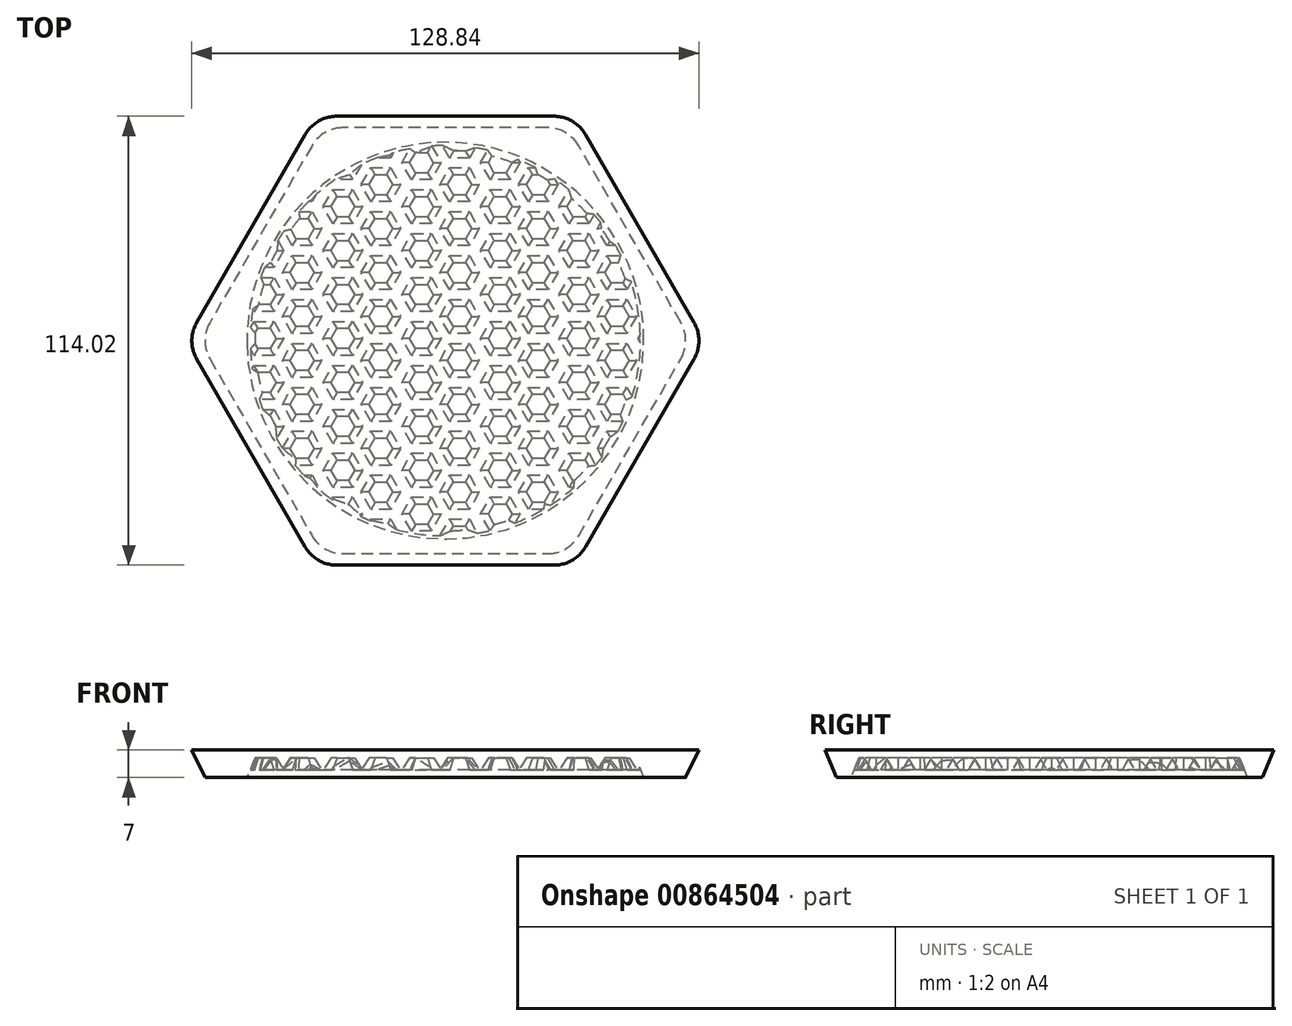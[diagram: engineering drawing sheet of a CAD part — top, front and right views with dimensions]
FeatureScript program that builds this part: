
annotation { "Feature Type Name" : "Feature", "Feature Type Description" : "" }
export const myFeature = defineFeature(function(context is Context, id is Id, definition is map)
    precondition{}
    {
        {
            var Q0;
            Q0=qCreatedBy(makeId("Top.planeOp"),FACE);
            var sketch = newSketch(context, id + "F0", { "sketchPlane" : qUnion([Q0])});
            skCircle(sketch, "E0.cCircle", {"center": v(0, 0) * mm, "radius": 62.5 * mm, "construction": true});
            skLineSegment(sketch, "E0.0", {"start": v(62.5, 0) * mm, "end": v(31.25, -54.13) * mm});
            skLineSegment(sketch, "E0.1", {"start": v(31.25, -54.13) * mm, "end": v(-31.25, -54.13) * mm});
            skLineSegment(sketch, "E0.2", {"start": v(-31.25, -54.13) * mm, "end": v(-62.5, 0) * mm});
            skLineSegment(sketch, "E0.3", {"start": v(-62.5, 0) * mm, "end": v(-31.25, 54.13) * mm});
            skLineSegment(sketch, "E0.4", {"start": v(-31.25, 54.13) * mm, "end": v(31.25, 54.13) * mm});
            skLineSegment(sketch, "E0.5", {"start": v(31.25, 54.13) * mm, "end": v(62.5, 0) * mm});
            skSolve(sketch);
        }
        {
            var Q0;
            Q0 = qSketchRegion(id + "F0", true);
            extrude(context, id + "F1", {"entities" : qUnion([Q0]), "depth" : 5 * mm, "offsetDistance" : 25 * mm, "hasDraft" : true, "draftAngle" : 30 * degree});
        }
        {
            var Q0;
            Q0=makeQuery(id+"F1.opExtrude","CAP_FACE",FACE,{"disambiguationData":[OSD([sQuery(id+"F0.wireOp",EDGE,"E0.0"),sQuery(id+"F0.wireOp",EDGE,"E0.1"),sQuery(id+"F0.wireOp",EDGE,"E0.2"),sQuery(id+"F0.wireOp",EDGE,"E0.3"),sQuery(id+"F0.wireOp",EDGE,"E0.4"),sQuery(id+"F0.wireOp",EDGE,"E0.5")])],"isStart":true});
            var sketch = newSketch(context, id + "F2", { "sketchPlane" : qUnion([Q0])});
            skCircle(sketch, "E1.cCircle", {"center": v(63.6, 60.82) * mm, "radius": 5 * mm, "construction": true});
            skLineSegment(sketch, "E1.0", {"start": v(58.6, 60.82) * mm, "end": v(61.1, 65.15) * mm});
            skLineSegment(sketch, "E1.1", {"start": v(61.1, 65.15) * mm, "end": v(66.1, 65.15) * mm});
            skLineSegment(sketch, "E1.2", {"start": v(66.1, 65.15) * mm, "end": v(68.6, 60.82) * mm});
            skLineSegment(sketch, "E1.3", {"start": v(68.6, 60.82) * mm, "end": v(66.1, 56.49) * mm});
            skLineSegment(sketch, "E1.4", {"start": v(66.1, 56.49) * mm, "end": v(61.1, 56.49) * mm});
            skLineSegment(sketch, "E1.5", {"start": v(61.1, 56.49) * mm, "end": v(58.6, 60.82) * mm});
            skCircle(sketch, "E2.cCircle", {"center": v(53.94, 66.4) * mm, "radius": 5 * mm, "construction": true});
            skLineSegment(sketch, "E2.0", {"start": v(48.94, 66.4) * mm, "end": v(51.44, 70.73) * mm});
            skLineSegment(sketch, "E2.1", {"start": v(51.44, 70.73) * mm, "end": v(56.44, 70.73) * mm});
            skLineSegment(sketch, "E2.2", {"start": v(56.44, 70.73) * mm, "end": v(58.94, 66.4) * mm});
            skLineSegment(sketch, "E2.3", {"start": v(58.94, 66.4) * mm, "end": v(56.44, 62.07) * mm});
            skLineSegment(sketch, "E2.4", {"start": v(56.44, 62.07) * mm, "end": v(51.44, 62.07) * mm});
            skLineSegment(sketch, "E2.5", {"start": v(51.44, 62.07) * mm, "end": v(48.94, 66.4) * mm});
            skLineSegment(sketch, "E3.0.1.0", {"start": v(51.44, 50.9) * mm, "end": v(48.94, 55.24) * mm});
            skCircle(sketch, "E3.0.1.1", {"center": v(63.6, 49.66) * mm, "radius": 5 * mm, "construction": true});
            skLineSegment(sketch, "E3.0.1.2", {"start": v(61.1, 53.99) * mm, "end": v(66.1, 53.99) * mm});
            skLineSegment(sketch, "E3.0.1.3", {"start": v(68.6, 49.66) * mm, "end": v(66.1, 45.33) * mm});
            skLineSegment(sketch, "E3.0.1.4", {"start": v(58.94, 55.24) * mm, "end": v(56.44, 50.9) * mm});
            skLineSegment(sketch, "E3.0.1.5", {"start": v(56.44, 59.57) * mm, "end": v(58.94, 55.24) * mm});
            skLineSegment(sketch, "E3.0.1.6", {"start": v(51.44, 59.57) * mm, "end": v(56.44, 59.57) * mm});
            skLineSegment(sketch, "E3.0.1.7", {"start": v(56.44, 50.9) * mm, "end": v(51.44, 50.9) * mm});
            skLineSegment(sketch, "E3.0.1.8", {"start": v(66.1, 53.99) * mm, "end": v(68.6, 49.66) * mm});
            skCircle(sketch, "E3.0.1.9", {"center": v(53.94, 55.24) * mm, "radius": 5 * mm, "construction": true});
            skLineSegment(sketch, "E3.0.1.10", {"start": v(48.94, 55.24) * mm, "end": v(51.44, 59.57) * mm});
            skLineSegment(sketch, "E3.0.1.11", {"start": v(61.1, 45.33) * mm, "end": v(58.6, 49.66) * mm});
            skLineSegment(sketch, "E3.0.1.12", {"start": v(66.1, 45.33) * mm, "end": v(61.1, 45.33) * mm});
            skLineSegment(sketch, "E3.0.1.13", {"start": v(58.6, 49.66) * mm, "end": v(61.1, 53.99) * mm});
            skLineSegment(sketch, "E3.0.2.0", {"start": v(51.44, 39.75) * mm, "end": v(48.94, 44.08) * mm});
            skCircle(sketch, "E3.0.2.1", {"center": v(63.6, 38.5) * mm, "radius": 5 * mm, "construction": true});
            skLineSegment(sketch, "E3.0.2.2", {"start": v(61.1, 42.83) * mm, "end": v(66.1, 42.83) * mm});
            skLineSegment(sketch, "E3.0.2.3", {"start": v(68.6, 38.5) * mm, "end": v(66.1, 34.17) * mm});
            skLineSegment(sketch, "E3.0.2.4", {"start": v(58.94, 44.08) * mm, "end": v(56.44, 39.75) * mm});
            skLineSegment(sketch, "E3.0.2.5", {"start": v(56.44, 48.4) * mm, "end": v(58.94, 44.08) * mm});
            skLineSegment(sketch, "E3.0.2.6", {"start": v(51.44, 48.4) * mm, "end": v(56.44, 48.4) * mm});
            skLineSegment(sketch, "E3.0.2.7", {"start": v(56.44, 39.75) * mm, "end": v(51.44, 39.75) * mm});
            skLineSegment(sketch, "E3.0.2.8", {"start": v(66.1, 42.83) * mm, "end": v(68.6, 38.5) * mm});
            skCircle(sketch, "E3.0.2.9", {"center": v(53.94, 44.08) * mm, "radius": 5 * mm, "construction": true});
            skLineSegment(sketch, "E3.0.2.10", {"start": v(48.94, 44.08) * mm, "end": v(51.44, 48.4) * mm});
            skLineSegment(sketch, "E3.0.2.11", {"start": v(61.1, 34.17) * mm, "end": v(58.6, 38.5) * mm});
            skLineSegment(sketch, "E3.0.2.12", {"start": v(66.1, 34.17) * mm, "end": v(61.1, 34.17) * mm});
            skLineSegment(sketch, "E3.0.2.13", {"start": v(58.6, 38.5) * mm, "end": v(61.1, 42.83) * mm});
            skLineSegment(sketch, "E3.0.3.0", {"start": v(51.44, 28.59) * mm, "end": v(48.94, 32.92) * mm});
            skCircle(sketch, "E3.0.3.1", {"center": v(63.6, 27.34) * mm, "radius": 5 * mm, "construction": true});
            skLineSegment(sketch, "E3.0.3.2", {"start": v(61.1, 31.67) * mm, "end": v(66.1, 31.67) * mm});
            skLineSegment(sketch, "E3.0.3.3", {"start": v(68.6, 27.34) * mm, "end": v(66.1, 23) * mm});
            skLineSegment(sketch, "E3.0.3.4", {"start": v(58.94, 32.92) * mm, "end": v(56.44, 28.59) * mm});
            skLineSegment(sketch, "E3.0.3.5", {"start": v(56.44, 37.25) * mm, "end": v(58.94, 32.92) * mm});
            skLineSegment(sketch, "E3.0.3.6", {"start": v(51.44, 37.25) * mm, "end": v(56.44, 37.25) * mm});
            skLineSegment(sketch, "E3.0.3.7", {"start": v(56.44, 28.59) * mm, "end": v(51.44, 28.59) * mm});
            skLineSegment(sketch, "E3.0.3.8", {"start": v(66.1, 31.67) * mm, "end": v(68.6, 27.34) * mm});
            skCircle(sketch, "E3.0.3.9", {"center": v(53.94, 32.92) * mm, "radius": 5 * mm, "construction": true});
            skLineSegment(sketch, "E3.0.3.10", {"start": v(48.94, 32.92) * mm, "end": v(51.44, 37.25) * mm});
            skLineSegment(sketch, "E3.0.3.11", {"start": v(61.1, 23) * mm, "end": v(58.6, 27.34) * mm});
            skLineSegment(sketch, "E3.0.3.12", {"start": v(66.1, 23) * mm, "end": v(61.1, 23) * mm});
            skLineSegment(sketch, "E3.0.3.13", {"start": v(58.6, 27.34) * mm, "end": v(61.1, 31.67) * mm});
            skLineSegment(sketch, "E3.0.4.0", {"start": v(51.44, 17.43) * mm, "end": v(48.94, 21.76) * mm});
            skCircle(sketch, "E3.0.4.1", {"center": v(63.6, 16.18) * mm, "radius": 5 * mm, "construction": true});
            skLineSegment(sketch, "E3.0.4.2", {"start": v(61.1, 20.5) * mm, "end": v(66.1, 20.5) * mm});
            skLineSegment(sketch, "E3.0.4.3", {"start": v(68.6, 16.18) * mm, "end": v(66.1, 11.85) * mm});
            skLineSegment(sketch, "E3.0.4.4", {"start": v(58.94, 21.76) * mm, "end": v(56.44, 17.43) * mm});
            skLineSegment(sketch, "E3.0.4.5", {"start": v(56.44, 26.09) * mm, "end": v(58.94, 21.76) * mm});
            skLineSegment(sketch, "E3.0.4.6", {"start": v(51.44, 26.09) * mm, "end": v(56.44, 26.09) * mm});
            skLineSegment(sketch, "E3.0.4.7", {"start": v(56.44, 17.43) * mm, "end": v(51.44, 17.43) * mm});
            skLineSegment(sketch, "E3.0.4.8", {"start": v(66.1, 20.5) * mm, "end": v(68.6, 16.18) * mm});
            skCircle(sketch, "E3.0.4.9", {"center": v(53.94, 21.76) * mm, "radius": 5 * mm, "construction": true});
            skLineSegment(sketch, "E3.0.4.10", {"start": v(48.94, 21.76) * mm, "end": v(51.44, 26.09) * mm});
            skLineSegment(sketch, "E3.0.4.11", {"start": v(61.1, 11.85) * mm, "end": v(58.6, 16.18) * mm});
            skLineSegment(sketch, "E3.0.4.12", {"start": v(66.1, 11.85) * mm, "end": v(61.1, 11.85) * mm});
            skLineSegment(sketch, "E3.0.4.13", {"start": v(58.6, 16.18) * mm, "end": v(61.1, 20.5) * mm});
            skLineSegment(sketch, "E3.0.5.0", {"start": v(51.44, 6.27) * mm, "end": v(48.94, 10.6) * mm});
            skCircle(sketch, "E3.0.5.1", {"center": v(63.6, 5.02) * mm, "radius": 5 * mm, "construction": true});
            skLineSegment(sketch, "E3.0.5.2", {"start": v(61.1, 9.35) * mm, "end": v(66.1, 9.35) * mm});
            skLineSegment(sketch, "E3.0.5.3", {"start": v(68.6, 5.02) * mm, "end": v(66.1, 0.69) * mm});
            skLineSegment(sketch, "E3.0.5.4", {"start": v(58.94, 10.6) * mm, "end": v(56.44, 6.27) * mm});
            skLineSegment(sketch, "E3.0.5.5", {"start": v(56.44, 14.93) * mm, "end": v(58.94, 10.6) * mm});
            skLineSegment(sketch, "E3.0.5.6", {"start": v(51.44, 14.93) * mm, "end": v(56.44, 14.93) * mm});
            skLineSegment(sketch, "E3.0.5.7", {"start": v(56.44, 6.27) * mm, "end": v(51.44, 6.27) * mm});
            skLineSegment(sketch, "E3.0.5.8", {"start": v(66.1, 9.35) * mm, "end": v(68.6, 5.02) * mm});
            skCircle(sketch, "E3.0.5.9", {"center": v(53.94, 10.6) * mm, "radius": 5 * mm, "construction": true});
            skLineSegment(sketch, "E3.0.5.10", {"start": v(48.94, 10.6) * mm, "end": v(51.44, 14.93) * mm});
            skLineSegment(sketch, "E3.0.5.11", {"start": v(61.1, 0.69) * mm, "end": v(58.6, 5.02) * mm});
            skLineSegment(sketch, "E3.0.5.12", {"start": v(66.1, 0.69) * mm, "end": v(61.1, 0.69) * mm});
            skLineSegment(sketch, "E3.0.5.13", {"start": v(58.6, 5.02) * mm, "end": v(61.1, 9.35) * mm});
            skLineSegment(sketch, "E3.0.6.0", {"start": v(51.44, -4.9) * mm, "end": v(48.94, -0.56) * mm});
            skCircle(sketch, "E3.0.6.1", {"center": v(63.6, -6.14) * mm, "radius": 5 * mm, "construction": true});
            skLineSegment(sketch, "E3.0.6.2", {"start": v(61.1, -1.81) * mm, "end": v(66.1, -1.81) * mm});
            skLineSegment(sketch, "E3.0.6.3", {"start": v(68.6, -6.14) * mm, "end": v(66.1, -10.47) * mm});
            skLineSegment(sketch, "E3.0.6.4", {"start": v(58.94, -0.56) * mm, "end": v(56.44, -4.9) * mm});
            skLineSegment(sketch, "E3.0.6.5", {"start": v(56.44, 3.77) * mm, "end": v(58.94, -0.56) * mm});
            skLineSegment(sketch, "E3.0.6.6", {"start": v(51.44, 3.77) * mm, "end": v(56.44, 3.77) * mm});
            skLineSegment(sketch, "E3.0.6.7", {"start": v(56.44, -4.9) * mm, "end": v(51.44, -4.9) * mm});
            skLineSegment(sketch, "E3.0.6.8", {"start": v(66.1, -1.81) * mm, "end": v(68.6, -6.14) * mm});
            skCircle(sketch, "E3.0.6.9", {"center": v(53.94, -0.56) * mm, "radius": 5 * mm, "construction": true});
            skLineSegment(sketch, "E3.0.6.10", {"start": v(48.94, -0.56) * mm, "end": v(51.44, 3.77) * mm});
            skLineSegment(sketch, "E3.0.6.11", {"start": v(61.1, -10.47) * mm, "end": v(58.6, -6.14) * mm});
            skLineSegment(sketch, "E3.0.6.12", {"start": v(66.1, -10.47) * mm, "end": v(61.1, -10.47) * mm});
            skLineSegment(sketch, "E3.0.6.13", {"start": v(58.6, -6.14) * mm, "end": v(61.1, -1.81) * mm});
            skLineSegment(sketch, "E3.0.7.0", {"start": v(51.44, -16.05) * mm, "end": v(48.94, -11.72) * mm});
            skCircle(sketch, "E3.0.7.1", {"center": v(63.6, -17.3) * mm, "radius": 5 * mm, "construction": true});
            skLineSegment(sketch, "E3.0.7.2", {"start": v(61.1, -12.97) * mm, "end": v(66.1, -12.97) * mm});
            skLineSegment(sketch, "E3.0.7.3", {"start": v(68.6, -17.3) * mm, "end": v(66.1, -21.63) * mm});
            skLineSegment(sketch, "E3.0.7.4", {"start": v(58.94, -11.72) * mm, "end": v(56.44, -16.05) * mm});
            skLineSegment(sketch, "E3.0.7.5", {"start": v(56.44, -7.4) * mm, "end": v(58.94, -11.72) * mm});
            skLineSegment(sketch, "E3.0.7.6", {"start": v(51.44, -7.4) * mm, "end": v(56.44, -7.4) * mm});
            skLineSegment(sketch, "E3.0.7.7", {"start": v(56.44, -16.05) * mm, "end": v(51.44, -16.05) * mm});
            skLineSegment(sketch, "E3.0.7.8", {"start": v(66.1, -12.97) * mm, "end": v(68.6, -17.3) * mm});
            skCircle(sketch, "E3.0.7.9", {"center": v(53.94, -11.72) * mm, "radius": 5 * mm, "construction": true});
            skLineSegment(sketch, "E3.0.7.10", {"start": v(48.94, -11.72) * mm, "end": v(51.44, -7.4) * mm});
            skLineSegment(sketch, "E3.0.7.11", {"start": v(61.1, -21.63) * mm, "end": v(58.6, -17.3) * mm});
            skLineSegment(sketch, "E3.0.7.12", {"start": v(66.1, -21.63) * mm, "end": v(61.1, -21.63) * mm});
            skLineSegment(sketch, "E3.0.7.13", {"start": v(58.6, -17.3) * mm, "end": v(61.1, -12.97) * mm});
            skLineSegment(sketch, "E3.0.8.0", {"start": v(51.44, -27.21) * mm, "end": v(48.94, -22.88) * mm});
            skCircle(sketch, "E3.0.8.1", {"center": v(63.6, -28.46) * mm, "radius": 5 * mm, "construction": true});
            skLineSegment(sketch, "E3.0.8.2", {"start": v(61.1, -24.13) * mm, "end": v(66.1, -24.13) * mm});
            skLineSegment(sketch, "E3.0.8.3", {"start": v(68.6, -28.46) * mm, "end": v(66.1, -32.8) * mm});
            skLineSegment(sketch, "E3.0.8.4", {"start": v(58.94, -22.88) * mm, "end": v(56.44, -27.21) * mm});
            skLineSegment(sketch, "E3.0.8.5", {"start": v(56.44, -18.55) * mm, "end": v(58.94, -22.88) * mm});
            skLineSegment(sketch, "E3.0.8.6", {"start": v(51.44, -18.55) * mm, "end": v(56.44, -18.55) * mm});
            skLineSegment(sketch, "E3.0.8.7", {"start": v(56.44, -27.21) * mm, "end": v(51.44, -27.21) * mm});
            skLineSegment(sketch, "E3.0.8.8", {"start": v(66.1, -24.13) * mm, "end": v(68.6, -28.46) * mm});
            skCircle(sketch, "E3.0.8.9", {"center": v(53.94, -22.88) * mm, "radius": 5 * mm, "construction": true});
            skLineSegment(sketch, "E3.0.8.10", {"start": v(48.94, -22.88) * mm, "end": v(51.44, -18.55) * mm});
            skLineSegment(sketch, "E3.0.8.11", {"start": v(61.1, -32.8) * mm, "end": v(58.6, -28.46) * mm});
            skLineSegment(sketch, "E3.0.8.12", {"start": v(66.1, -32.8) * mm, "end": v(61.1, -32.8) * mm});
            skLineSegment(sketch, "E3.0.8.13", {"start": v(58.6, -28.46) * mm, "end": v(61.1, -24.13) * mm});
            skLineSegment(sketch, "E3.0.9.0", {"start": v(51.44, -38.37) * mm, "end": v(48.94, -34.04) * mm});
            skCircle(sketch, "E3.0.9.1", {"center": v(63.6, -39.62) * mm, "radius": 5 * mm, "construction": true});
            skLineSegment(sketch, "E3.0.9.2", {"start": v(61.1, -35.3) * mm, "end": v(66.1, -35.3) * mm});
            skLineSegment(sketch, "E3.0.9.3", {"start": v(68.6, -39.62) * mm, "end": v(66.1, -43.95) * mm});
            skLineSegment(sketch, "E3.0.9.4", {"start": v(58.94, -34.04) * mm, "end": v(56.44, -38.37) * mm});
            skLineSegment(sketch, "E3.0.9.5", {"start": v(56.44, -29.71) * mm, "end": v(58.94, -34.04) * mm});
            skLineSegment(sketch, "E3.0.9.6", {"start": v(51.44, -29.71) * mm, "end": v(56.44, -29.71) * mm});
            skLineSegment(sketch, "E3.0.9.7", {"start": v(56.44, -38.37) * mm, "end": v(51.44, -38.37) * mm});
            skLineSegment(sketch, "E3.0.9.8", {"start": v(66.1, -35.3) * mm, "end": v(68.6, -39.62) * mm});
            skCircle(sketch, "E3.0.9.9", {"center": v(53.94, -34.04) * mm, "radius": 5 * mm, "construction": true});
            skLineSegment(sketch, "E3.0.9.10", {"start": v(48.94, -34.04) * mm, "end": v(51.44, -29.71) * mm});
            skLineSegment(sketch, "E3.0.9.11", {"start": v(61.1, -43.95) * mm, "end": v(58.6, -39.62) * mm});
            skLineSegment(sketch, "E3.0.9.12", {"start": v(66.1, -43.95) * mm, "end": v(61.1, -43.95) * mm});
            skLineSegment(sketch, "E3.0.9.13", {"start": v(58.6, -39.62) * mm, "end": v(61.1, -35.3) * mm});
            skLineSegment(sketch, "E3.0.10.0", {"start": v(51.44, -49.53) * mm, "end": v(48.94, -45.2) * mm});
            skCircle(sketch, "E3.0.10.1", {"center": v(63.6, -50.78) * mm, "radius": 5 * mm, "construction": true});
            skLineSegment(sketch, "E3.0.10.2", {"start": v(61.1, -46.45) * mm, "end": v(66.1, -46.45) * mm});
            skLineSegment(sketch, "E3.0.10.3", {"start": v(68.6, -50.78) * mm, "end": v(66.1, -55.11) * mm});
            skLineSegment(sketch, "E3.0.10.4", {"start": v(58.94, -45.2) * mm, "end": v(56.44, -49.53) * mm});
            skLineSegment(sketch, "E3.0.10.5", {"start": v(56.44, -40.87) * mm, "end": v(58.94, -45.2) * mm});
            skLineSegment(sketch, "E3.0.10.6", {"start": v(51.44, -40.87) * mm, "end": v(56.44, -40.87) * mm});
            skLineSegment(sketch, "E3.0.10.7", {"start": v(56.44, -49.53) * mm, "end": v(51.44, -49.53) * mm});
            skLineSegment(sketch, "E3.0.10.8", {"start": v(66.1, -46.45) * mm, "end": v(68.6, -50.78) * mm});
            skCircle(sketch, "E3.0.10.9", {"center": v(53.94, -45.2) * mm, "radius": 5 * mm, "construction": true});
            skLineSegment(sketch, "E3.0.10.10", {"start": v(48.94, -45.2) * mm, "end": v(51.44, -40.87) * mm});
            skLineSegment(sketch, "E3.0.10.11", {"start": v(61.1, -55.11) * mm, "end": v(58.6, -50.78) * mm});
            skLineSegment(sketch, "E3.0.10.12", {"start": v(66.1, -55.11) * mm, "end": v(61.1, -55.11) * mm});
            skLineSegment(sketch, "E3.0.10.13", {"start": v(58.6, -50.78) * mm, "end": v(61.1, -46.45) * mm});
            skLineSegment(sketch, "E3.1.0.0", {"start": v(31.44, 62.07) * mm, "end": v(28.94, 66.4) * mm});
            skCircle(sketch, "E3.1.0.1", {"center": v(43.6, 60.82) * mm, "radius": 5 * mm, "construction": true});
            skLineSegment(sketch, "E3.1.0.2", {"start": v(41.1, 65.15) * mm, "end": v(46.1, 65.15) * mm});
            skLineSegment(sketch, "E3.1.0.3", {"start": v(48.6, 60.82) * mm, "end": v(46.1, 56.49) * mm});
            skLineSegment(sketch, "E3.1.0.4", {"start": v(38.94, 66.4) * mm, "end": v(36.44, 62.07) * mm});
            skLineSegment(sketch, "E3.1.0.5", {"start": v(36.44, 70.73) * mm, "end": v(38.94, 66.4) * mm});
            skLineSegment(sketch, "E3.1.0.6", {"start": v(31.44, 70.73) * mm, "end": v(36.44, 70.73) * mm});
            skLineSegment(sketch, "E3.1.0.7", {"start": v(36.44, 62.07) * mm, "end": v(31.44, 62.07) * mm});
            skLineSegment(sketch, "E3.1.0.8", {"start": v(46.1, 65.15) * mm, "end": v(48.6, 60.82) * mm});
            skCircle(sketch, "E3.1.0.9", {"center": v(33.94, 66.4) * mm, "radius": 5 * mm, "construction": true});
            skLineSegment(sketch, "E3.1.0.10", {"start": v(28.94, 66.4) * mm, "end": v(31.44, 70.73) * mm});
            skLineSegment(sketch, "E3.1.0.11", {"start": v(41.1, 56.49) * mm, "end": v(38.6, 60.82) * mm});
            skLineSegment(sketch, "E3.1.0.12", {"start": v(46.1, 56.49) * mm, "end": v(41.1, 56.49) * mm});
            skLineSegment(sketch, "E3.1.0.13", {"start": v(38.6, 60.82) * mm, "end": v(41.1, 65.15) * mm});
            skLineSegment(sketch, "E3.1.1.0", {"start": v(31.44, 50.9) * mm, "end": v(28.94, 55.24) * mm});
            skCircle(sketch, "E3.1.1.1", {"center": v(43.6, 49.66) * mm, "radius": 5 * mm, "construction": true});
            skLineSegment(sketch, "E3.1.1.2", {"start": v(41.1, 53.99) * mm, "end": v(46.1, 53.99) * mm});
            skLineSegment(sketch, "E3.1.1.3", {"start": v(48.6, 49.66) * mm, "end": v(46.1, 45.33) * mm});
            skLineSegment(sketch, "E3.1.1.4", {"start": v(38.94, 55.24) * mm, "end": v(36.44, 50.9) * mm});
            skLineSegment(sketch, "E3.1.1.5", {"start": v(36.44, 59.57) * mm, "end": v(38.94, 55.24) * mm});
            skLineSegment(sketch, "E3.1.1.6", {"start": v(31.44, 59.57) * mm, "end": v(36.44, 59.57) * mm});
            skLineSegment(sketch, "E3.1.1.7", {"start": v(36.44, 50.9) * mm, "end": v(31.44, 50.9) * mm});
            skLineSegment(sketch, "E3.1.1.8", {"start": v(46.1, 53.99) * mm, "end": v(48.6, 49.66) * mm});
            skCircle(sketch, "E3.1.1.9", {"center": v(33.94, 55.24) * mm, "radius": 5 * mm, "construction": true});
            skLineSegment(sketch, "E3.1.1.10", {"start": v(28.94, 55.24) * mm, "end": v(31.44, 59.57) * mm});
            skLineSegment(sketch, "E3.1.1.11", {"start": v(41.1, 45.33) * mm, "end": v(38.6, 49.66) * mm});
            skLineSegment(sketch, "E3.1.1.12", {"start": v(46.1, 45.33) * mm, "end": v(41.1, 45.33) * mm});
            skLineSegment(sketch, "E3.1.1.13", {"start": v(38.6, 49.66) * mm, "end": v(41.1, 53.99) * mm});
            skLineSegment(sketch, "E3.1.2.0", {"start": v(31.44, 39.75) * mm, "end": v(28.94, 44.08) * mm});
            skCircle(sketch, "E3.1.2.1", {"center": v(43.6, 38.5) * mm, "radius": 5 * mm, "construction": true});
            skLineSegment(sketch, "E3.1.2.2", {"start": v(41.1, 42.83) * mm, "end": v(46.1, 42.83) * mm});
            skLineSegment(sketch, "E3.1.2.3", {"start": v(48.6, 38.5) * mm, "end": v(46.1, 34.17) * mm});
            skLineSegment(sketch, "E3.1.2.4", {"start": v(38.94, 44.08) * mm, "end": v(36.44, 39.75) * mm});
            skLineSegment(sketch, "E3.1.2.5", {"start": v(36.44, 48.4) * mm, "end": v(38.94, 44.08) * mm});
            skLineSegment(sketch, "E3.1.2.6", {"start": v(31.44, 48.4) * mm, "end": v(36.44, 48.4) * mm});
            skLineSegment(sketch, "E3.1.2.7", {"start": v(36.44, 39.75) * mm, "end": v(31.44, 39.75) * mm});
            skLineSegment(sketch, "E3.1.2.8", {"start": v(46.1, 42.83) * mm, "end": v(48.6, 38.5) * mm});
            skCircle(sketch, "E3.1.2.9", {"center": v(33.94, 44.08) * mm, "radius": 5 * mm, "construction": true});
            skLineSegment(sketch, "E3.1.2.10", {"start": v(28.94, 44.08) * mm, "end": v(31.44, 48.4) * mm});
            skLineSegment(sketch, "E3.1.2.11", {"start": v(41.1, 34.17) * mm, "end": v(38.6, 38.5) * mm});
            skLineSegment(sketch, "E3.1.2.12", {"start": v(46.1, 34.17) * mm, "end": v(41.1, 34.17) * mm});
            skLineSegment(sketch, "E3.1.2.13", {"start": v(38.6, 38.5) * mm, "end": v(41.1, 42.83) * mm});
            skLineSegment(sketch, "E3.1.3.0", {"start": v(31.44, 28.59) * mm, "end": v(28.94, 32.92) * mm});
            skCircle(sketch, "E3.1.3.1", {"center": v(43.6, 27.34) * mm, "radius": 5 * mm, "construction": true});
            skLineSegment(sketch, "E3.1.3.2", {"start": v(41.1, 31.67) * mm, "end": v(46.1, 31.67) * mm});
            skLineSegment(sketch, "E3.1.3.3", {"start": v(48.6, 27.34) * mm, "end": v(46.1, 23) * mm});
            skLineSegment(sketch, "E3.1.3.4", {"start": v(38.94, 32.92) * mm, "end": v(36.44, 28.59) * mm});
            skLineSegment(sketch, "E3.1.3.5", {"start": v(36.44, 37.25) * mm, "end": v(38.94, 32.92) * mm});
            skLineSegment(sketch, "E3.1.3.6", {"start": v(31.44, 37.25) * mm, "end": v(36.44, 37.25) * mm});
            skLineSegment(sketch, "E3.1.3.7", {"start": v(36.44, 28.59) * mm, "end": v(31.44, 28.59) * mm});
            skLineSegment(sketch, "E3.1.3.8", {"start": v(46.1, 31.67) * mm, "end": v(48.6, 27.34) * mm});
            skCircle(sketch, "E3.1.3.9", {"center": v(33.94, 32.92) * mm, "radius": 5 * mm, "construction": true});
            skLineSegment(sketch, "E3.1.3.10", {"start": v(28.94, 32.92) * mm, "end": v(31.44, 37.25) * mm});
            skLineSegment(sketch, "E3.1.3.11", {"start": v(41.1, 23) * mm, "end": v(38.6, 27.34) * mm});
            skLineSegment(sketch, "E3.1.3.12", {"start": v(46.1, 23) * mm, "end": v(41.1, 23) * mm});
            skLineSegment(sketch, "E3.1.3.13", {"start": v(38.6, 27.34) * mm, "end": v(41.1, 31.67) * mm});
            skLineSegment(sketch, "E3.1.4.0", {"start": v(31.44, 17.43) * mm, "end": v(28.94, 21.76) * mm});
            skCircle(sketch, "E3.1.4.1", {"center": v(43.6, 16.18) * mm, "radius": 5 * mm, "construction": true});
            skLineSegment(sketch, "E3.1.4.2", {"start": v(41.1, 20.5) * mm, "end": v(46.1, 20.5) * mm});
            skLineSegment(sketch, "E3.1.4.3", {"start": v(48.6, 16.18) * mm, "end": v(46.1, 11.85) * mm});
            skLineSegment(sketch, "E3.1.4.4", {"start": v(38.94, 21.76) * mm, "end": v(36.44, 17.43) * mm});
            skLineSegment(sketch, "E3.1.4.5", {"start": v(36.44, 26.09) * mm, "end": v(38.94, 21.76) * mm});
            skLineSegment(sketch, "E3.1.4.6", {"start": v(31.44, 26.09) * mm, "end": v(36.44, 26.09) * mm});
            skLineSegment(sketch, "E3.1.4.7", {"start": v(36.44, 17.43) * mm, "end": v(31.44, 17.43) * mm});
            skLineSegment(sketch, "E3.1.4.8", {"start": v(46.1, 20.5) * mm, "end": v(48.6, 16.18) * mm});
            skCircle(sketch, "E3.1.4.9", {"center": v(33.94, 21.76) * mm, "radius": 5 * mm, "construction": true});
            skLineSegment(sketch, "E3.1.4.10", {"start": v(28.94, 21.76) * mm, "end": v(31.44, 26.09) * mm});
            skLineSegment(sketch, "E3.1.4.11", {"start": v(41.1, 11.85) * mm, "end": v(38.6, 16.18) * mm});
            skLineSegment(sketch, "E3.1.4.12", {"start": v(46.1, 11.85) * mm, "end": v(41.1, 11.85) * mm});
            skLineSegment(sketch, "E3.1.4.13", {"start": v(38.6, 16.18) * mm, "end": v(41.1, 20.5) * mm});
            skLineSegment(sketch, "E3.1.5.0", {"start": v(31.44, 6.27) * mm, "end": v(28.94, 10.6) * mm});
            skCircle(sketch, "E3.1.5.1", {"center": v(43.6, 5.02) * mm, "radius": 5 * mm, "construction": true});
            skLineSegment(sketch, "E3.1.5.2", {"start": v(41.1, 9.35) * mm, "end": v(46.1, 9.35) * mm});
            skLineSegment(sketch, "E3.1.5.3", {"start": v(48.6, 5.02) * mm, "end": v(46.1, 0.69) * mm});
            skLineSegment(sketch, "E3.1.5.4", {"start": v(38.94, 10.6) * mm, "end": v(36.44, 6.27) * mm});
            skLineSegment(sketch, "E3.1.5.5", {"start": v(36.44, 14.93) * mm, "end": v(38.94, 10.6) * mm});
            skLineSegment(sketch, "E3.1.5.6", {"start": v(31.44, 14.93) * mm, "end": v(36.44, 14.93) * mm});
            skLineSegment(sketch, "E3.1.5.7", {"start": v(36.44, 6.27) * mm, "end": v(31.44, 6.27) * mm});
            skLineSegment(sketch, "E3.1.5.8", {"start": v(46.1, 9.35) * mm, "end": v(48.6, 5.02) * mm});
            skCircle(sketch, "E3.1.5.9", {"center": v(33.94, 10.6) * mm, "radius": 5 * mm, "construction": true});
            skLineSegment(sketch, "E3.1.5.10", {"start": v(28.94, 10.6) * mm, "end": v(31.44, 14.93) * mm});
            skLineSegment(sketch, "E3.1.5.11", {"start": v(41.1, 0.69) * mm, "end": v(38.6, 5.02) * mm});
            skLineSegment(sketch, "E3.1.5.12", {"start": v(46.1, 0.69) * mm, "end": v(41.1, 0.69) * mm});
            skLineSegment(sketch, "E3.1.5.13", {"start": v(38.6, 5.02) * mm, "end": v(41.1, 9.35) * mm});
            skLineSegment(sketch, "E3.1.6.0", {"start": v(31.44, -4.9) * mm, "end": v(28.94, -0.56) * mm});
            skCircle(sketch, "E3.1.6.1", {"center": v(43.6, -6.14) * mm, "radius": 5 * mm, "construction": true});
            skLineSegment(sketch, "E3.1.6.2", {"start": v(41.1, -1.81) * mm, "end": v(46.1, -1.81) * mm});
            skLineSegment(sketch, "E3.1.6.3", {"start": v(48.6, -6.14) * mm, "end": v(46.1, -10.47) * mm});
            skLineSegment(sketch, "E3.1.6.4", {"start": v(38.94, -0.56) * mm, "end": v(36.44, -4.9) * mm});
            skLineSegment(sketch, "E3.1.6.5", {"start": v(36.44, 3.77) * mm, "end": v(38.94, -0.56) * mm});
            skLineSegment(sketch, "E3.1.6.6", {"start": v(31.44, 3.77) * mm, "end": v(36.44, 3.77) * mm});
            skLineSegment(sketch, "E3.1.6.7", {"start": v(36.44, -4.9) * mm, "end": v(31.44, -4.9) * mm});
            skLineSegment(sketch, "E3.1.6.8", {"start": v(46.1, -1.81) * mm, "end": v(48.6, -6.14) * mm});
            skCircle(sketch, "E3.1.6.9", {"center": v(33.94, -0.56) * mm, "radius": 5 * mm, "construction": true});
            skLineSegment(sketch, "E3.1.6.10", {"start": v(28.94, -0.56) * mm, "end": v(31.44, 3.77) * mm});
            skLineSegment(sketch, "E3.1.6.11", {"start": v(41.1, -10.47) * mm, "end": v(38.6, -6.14) * mm});
            skLineSegment(sketch, "E3.1.6.12", {"start": v(46.1, -10.47) * mm, "end": v(41.1, -10.47) * mm});
            skLineSegment(sketch, "E3.1.6.13", {"start": v(38.6, -6.14) * mm, "end": v(41.1, -1.81) * mm});
            skLineSegment(sketch, "E3.1.7.0", {"start": v(31.44, -16.05) * mm, "end": v(28.94, -11.72) * mm});
            skCircle(sketch, "E3.1.7.1", {"center": v(43.6, -17.3) * mm, "radius": 5 * mm, "construction": true});
            skLineSegment(sketch, "E3.1.7.2", {"start": v(41.1, -12.97) * mm, "end": v(46.1, -12.97) * mm});
            skLineSegment(sketch, "E3.1.7.3", {"start": v(48.6, -17.3) * mm, "end": v(46.1, -21.63) * mm});
            skLineSegment(sketch, "E3.1.7.4", {"start": v(38.94, -11.72) * mm, "end": v(36.44, -16.05) * mm});
            skLineSegment(sketch, "E3.1.7.5", {"start": v(36.44, -7.4) * mm, "end": v(38.94, -11.72) * mm});
            skLineSegment(sketch, "E3.1.7.6", {"start": v(31.44, -7.4) * mm, "end": v(36.44, -7.4) * mm});
            skLineSegment(sketch, "E3.1.7.7", {"start": v(36.44, -16.05) * mm, "end": v(31.44, -16.05) * mm});
            skLineSegment(sketch, "E3.1.7.8", {"start": v(46.1, -12.97) * mm, "end": v(48.6, -17.3) * mm});
            skCircle(sketch, "E3.1.7.9", {"center": v(33.94, -11.72) * mm, "radius": 5 * mm, "construction": true});
            skLineSegment(sketch, "E3.1.7.10", {"start": v(28.94, -11.72) * mm, "end": v(31.44, -7.4) * mm});
            skLineSegment(sketch, "E3.1.7.11", {"start": v(41.1, -21.63) * mm, "end": v(38.6, -17.3) * mm});
            skLineSegment(sketch, "E3.1.7.12", {"start": v(46.1, -21.63) * mm, "end": v(41.1, -21.63) * mm});
            skLineSegment(sketch, "E3.1.7.13", {"start": v(38.6, -17.3) * mm, "end": v(41.1, -12.97) * mm});
            skLineSegment(sketch, "E3.1.8.0", {"start": v(31.44, -27.21) * mm, "end": v(28.94, -22.88) * mm});
            skCircle(sketch, "E3.1.8.1", {"center": v(43.6, -28.46) * mm, "radius": 5 * mm, "construction": true});
            skLineSegment(sketch, "E3.1.8.2", {"start": v(41.1, -24.13) * mm, "end": v(46.1, -24.13) * mm});
            skLineSegment(sketch, "E3.1.8.3", {"start": v(48.6, -28.46) * mm, "end": v(46.1, -32.8) * mm});
            skLineSegment(sketch, "E3.1.8.4", {"start": v(38.94, -22.88) * mm, "end": v(36.44, -27.21) * mm});
            skLineSegment(sketch, "E3.1.8.5", {"start": v(36.44, -18.55) * mm, "end": v(38.94, -22.88) * mm});
            skLineSegment(sketch, "E3.1.8.6", {"start": v(31.44, -18.55) * mm, "end": v(36.44, -18.55) * mm});
            skLineSegment(sketch, "E3.1.8.7", {"start": v(36.44, -27.21) * mm, "end": v(31.44, -27.21) * mm});
            skLineSegment(sketch, "E3.1.8.8", {"start": v(46.1, -24.13) * mm, "end": v(48.6, -28.46) * mm});
            skCircle(sketch, "E3.1.8.9", {"center": v(33.94, -22.88) * mm, "radius": 5 * mm, "construction": true});
            skLineSegment(sketch, "E3.1.8.10", {"start": v(28.94, -22.88) * mm, "end": v(31.44, -18.55) * mm});
            skLineSegment(sketch, "E3.1.8.11", {"start": v(41.1, -32.8) * mm, "end": v(38.6, -28.46) * mm});
            skLineSegment(sketch, "E3.1.8.12", {"start": v(46.1, -32.8) * mm, "end": v(41.1, -32.8) * mm});
            skLineSegment(sketch, "E3.1.8.13", {"start": v(38.6, -28.46) * mm, "end": v(41.1, -24.13) * mm});
            skLineSegment(sketch, "E3.1.9.0", {"start": v(31.44, -38.37) * mm, "end": v(28.94, -34.04) * mm});
            skCircle(sketch, "E3.1.9.1", {"center": v(43.6, -39.62) * mm, "radius": 5 * mm, "construction": true});
            skLineSegment(sketch, "E3.1.9.2", {"start": v(41.1, -35.3) * mm, "end": v(46.1, -35.3) * mm});
            skLineSegment(sketch, "E3.1.9.3", {"start": v(48.6, -39.62) * mm, "end": v(46.1, -43.95) * mm});
            skLineSegment(sketch, "E3.1.9.4", {"start": v(38.94, -34.04) * mm, "end": v(36.44, -38.37) * mm});
            skLineSegment(sketch, "E3.1.9.5", {"start": v(36.44, -29.71) * mm, "end": v(38.94, -34.04) * mm});
            skLineSegment(sketch, "E3.1.9.6", {"start": v(31.44, -29.71) * mm, "end": v(36.44, -29.71) * mm});
            skLineSegment(sketch, "E3.1.9.7", {"start": v(36.44, -38.37) * mm, "end": v(31.44, -38.37) * mm});
            skLineSegment(sketch, "E3.1.9.8", {"start": v(46.1, -35.3) * mm, "end": v(48.6, -39.62) * mm});
            skCircle(sketch, "E3.1.9.9", {"center": v(33.94, -34.04) * mm, "radius": 5 * mm, "construction": true});
            skLineSegment(sketch, "E3.1.9.10", {"start": v(28.94, -34.04) * mm, "end": v(31.44, -29.71) * mm});
            skLineSegment(sketch, "E3.1.9.11", {"start": v(41.1, -43.95) * mm, "end": v(38.6, -39.62) * mm});
            skLineSegment(sketch, "E3.1.9.12", {"start": v(46.1, -43.95) * mm, "end": v(41.1, -43.95) * mm});
            skLineSegment(sketch, "E3.1.9.13", {"start": v(38.6, -39.62) * mm, "end": v(41.1, -35.3) * mm});
            skLineSegment(sketch, "E3.1.10.0", {"start": v(31.44, -49.53) * mm, "end": v(28.94, -45.2) * mm});
            skCircle(sketch, "E3.1.10.1", {"center": v(43.6, -50.78) * mm, "radius": 5 * mm, "construction": true});
            skLineSegment(sketch, "E3.1.10.2", {"start": v(41.1, -46.45) * mm, "end": v(46.1, -46.45) * mm});
            skLineSegment(sketch, "E3.1.10.3", {"start": v(48.6, -50.78) * mm, "end": v(46.1, -55.11) * mm});
            skLineSegment(sketch, "E3.1.10.4", {"start": v(38.94, -45.2) * mm, "end": v(36.44, -49.53) * mm});
            skLineSegment(sketch, "E3.1.10.5", {"start": v(36.44, -40.87) * mm, "end": v(38.94, -45.2) * mm});
            skLineSegment(sketch, "E3.1.10.6", {"start": v(31.44, -40.87) * mm, "end": v(36.44, -40.87) * mm});
            skLineSegment(sketch, "E3.1.10.7", {"start": v(36.44, -49.53) * mm, "end": v(31.44, -49.53) * mm});
            skLineSegment(sketch, "E3.1.10.8", {"start": v(46.1, -46.45) * mm, "end": v(48.6, -50.78) * mm});
            skCircle(sketch, "E3.1.10.9", {"center": v(33.94, -45.2) * mm, "radius": 5 * mm, "construction": true});
            skLineSegment(sketch, "E3.1.10.10", {"start": v(28.94, -45.2) * mm, "end": v(31.44, -40.87) * mm});
            skLineSegment(sketch, "E3.1.10.11", {"start": v(41.1, -55.11) * mm, "end": v(38.6, -50.78) * mm});
            skLineSegment(sketch, "E3.1.10.12", {"start": v(46.1, -55.11) * mm, "end": v(41.1, -55.11) * mm});
            skLineSegment(sketch, "E3.1.10.13", {"start": v(38.6, -50.78) * mm, "end": v(41.1, -46.45) * mm});
            skLineSegment(sketch, "E3.2.0.0", {"start": v(11.44, 62.07) * mm, "end": v(8.94, 66.4) * mm});
            skCircle(sketch, "E3.2.0.1", {"center": v(23.6, 60.82) * mm, "radius": 5 * mm, "construction": true});
            skLineSegment(sketch, "E3.2.0.2", {"start": v(21.1, 65.15) * mm, "end": v(26.1, 65.15) * mm});
            skLineSegment(sketch, "E3.2.0.3", {"start": v(28.6, 60.82) * mm, "end": v(26.1, 56.49) * mm});
            skLineSegment(sketch, "E3.2.0.4", {"start": v(18.94, 66.4) * mm, "end": v(16.44, 62.07) * mm});
            skLineSegment(sketch, "E3.2.0.5", {"start": v(16.44, 70.73) * mm, "end": v(18.94, 66.4) * mm});
            skLineSegment(sketch, "E3.2.0.6", {"start": v(11.44, 70.73) * mm, "end": v(16.44, 70.73) * mm});
            skLineSegment(sketch, "E3.2.0.7", {"start": v(16.44, 62.07) * mm, "end": v(11.44, 62.07) * mm});
            skLineSegment(sketch, "E3.2.0.8", {"start": v(26.1, 65.15) * mm, "end": v(28.6, 60.82) * mm});
            skCircle(sketch, "E3.2.0.9", {"center": v(13.94, 66.4) * mm, "radius": 5 * mm, "construction": true});
            skLineSegment(sketch, "E3.2.0.10", {"start": v(8.94, 66.4) * mm, "end": v(11.44, 70.73) * mm});
            skLineSegment(sketch, "E3.2.0.11", {"start": v(21.1, 56.49) * mm, "end": v(18.6, 60.82) * mm});
            skLineSegment(sketch, "E3.2.0.12", {"start": v(26.1, 56.49) * mm, "end": v(21.1, 56.49) * mm});
            skLineSegment(sketch, "E3.2.0.13", {"start": v(18.6, 60.82) * mm, "end": v(21.1, 65.15) * mm});
            skLineSegment(sketch, "E3.2.1.0", {"start": v(11.44, 50.9) * mm, "end": v(8.94, 55.24) * mm});
            skCircle(sketch, "E3.2.1.1", {"center": v(23.6, 49.66) * mm, "radius": 5 * mm, "construction": true});
            skLineSegment(sketch, "E3.2.1.2", {"start": v(21.1, 53.99) * mm, "end": v(26.1, 53.99) * mm});
            skLineSegment(sketch, "E3.2.1.3", {"start": v(28.6, 49.66) * mm, "end": v(26.1, 45.33) * mm});
            skLineSegment(sketch, "E3.2.1.4", {"start": v(18.94, 55.24) * mm, "end": v(16.44, 50.9) * mm});
            skLineSegment(sketch, "E3.2.1.5", {"start": v(16.44, 59.57) * mm, "end": v(18.94, 55.24) * mm});
            skLineSegment(sketch, "E3.2.1.6", {"start": v(11.44, 59.57) * mm, "end": v(16.44, 59.57) * mm});
            skLineSegment(sketch, "E3.2.1.7", {"start": v(16.44, 50.9) * mm, "end": v(11.44, 50.9) * mm});
            skLineSegment(sketch, "E3.2.1.8", {"start": v(26.1, 53.99) * mm, "end": v(28.6, 49.66) * mm});
            skCircle(sketch, "E3.2.1.9", {"center": v(13.94, 55.24) * mm, "radius": 5 * mm, "construction": true});
            skLineSegment(sketch, "E3.2.1.10", {"start": v(8.94, 55.24) * mm, "end": v(11.44, 59.57) * mm});
            skLineSegment(sketch, "E3.2.1.11", {"start": v(21.1, 45.33) * mm, "end": v(18.6, 49.66) * mm});
            skLineSegment(sketch, "E3.2.1.12", {"start": v(26.1, 45.33) * mm, "end": v(21.1, 45.33) * mm});
            skLineSegment(sketch, "E3.2.1.13", {"start": v(18.6, 49.66) * mm, "end": v(21.1, 53.99) * mm});
            skLineSegment(sketch, "E3.2.2.0", {"start": v(11.44, 39.75) * mm, "end": v(8.94, 44.08) * mm});
            skCircle(sketch, "E3.2.2.1", {"center": v(23.6, 38.5) * mm, "radius": 5 * mm, "construction": true});
            skLineSegment(sketch, "E3.2.2.2", {"start": v(21.1, 42.83) * mm, "end": v(26.1, 42.83) * mm});
            skLineSegment(sketch, "E3.2.2.3", {"start": v(28.6, 38.5) * mm, "end": v(26.1, 34.17) * mm});
            skLineSegment(sketch, "E3.2.2.4", {"start": v(18.94, 44.08) * mm, "end": v(16.44, 39.75) * mm});
            skLineSegment(sketch, "E3.2.2.5", {"start": v(16.44, 48.4) * mm, "end": v(18.94, 44.08) * mm});
            skLineSegment(sketch, "E3.2.2.6", {"start": v(11.44, 48.4) * mm, "end": v(16.44, 48.4) * mm});
            skLineSegment(sketch, "E3.2.2.7", {"start": v(16.44, 39.75) * mm, "end": v(11.44, 39.75) * mm});
            skLineSegment(sketch, "E3.2.2.8", {"start": v(26.1, 42.83) * mm, "end": v(28.6, 38.5) * mm});
            skCircle(sketch, "E3.2.2.9", {"center": v(13.94, 44.08) * mm, "radius": 5 * mm, "construction": true});
            skLineSegment(sketch, "E3.2.2.10", {"start": v(8.94, 44.08) * mm, "end": v(11.44, 48.4) * mm});
            skLineSegment(sketch, "E3.2.2.11", {"start": v(21.1, 34.17) * mm, "end": v(18.6, 38.5) * mm});
            skLineSegment(sketch, "E3.2.2.12", {"start": v(26.1, 34.17) * mm, "end": v(21.1, 34.17) * mm});
            skLineSegment(sketch, "E3.2.2.13", {"start": v(18.6, 38.5) * mm, "end": v(21.1, 42.83) * mm});
            skLineSegment(sketch, "E3.2.3.0", {"start": v(11.44, 28.59) * mm, "end": v(8.94, 32.92) * mm});
            skCircle(sketch, "E3.2.3.1", {"center": v(23.6, 27.34) * mm, "radius": 5 * mm, "construction": true});
            skLineSegment(sketch, "E3.2.3.2", {"start": v(21.1, 31.67) * mm, "end": v(26.1, 31.67) * mm});
            skLineSegment(sketch, "E3.2.3.3", {"start": v(28.6, 27.34) * mm, "end": v(26.1, 23) * mm});
            skLineSegment(sketch, "E3.2.3.4", {"start": v(18.94, 32.92) * mm, "end": v(16.44, 28.59) * mm});
            skLineSegment(sketch, "E3.2.3.5", {"start": v(16.44, 37.25) * mm, "end": v(18.94, 32.92) * mm});
            skLineSegment(sketch, "E3.2.3.6", {"start": v(11.44, 37.25) * mm, "end": v(16.44, 37.25) * mm});
            skLineSegment(sketch, "E3.2.3.7", {"start": v(16.44, 28.59) * mm, "end": v(11.44, 28.59) * mm});
            skLineSegment(sketch, "E3.2.3.8", {"start": v(26.1, 31.67) * mm, "end": v(28.6, 27.34) * mm});
            skCircle(sketch, "E3.2.3.9", {"center": v(13.94, 32.92) * mm, "radius": 5 * mm, "construction": true});
            skLineSegment(sketch, "E3.2.3.10", {"start": v(8.94, 32.92) * mm, "end": v(11.44, 37.25) * mm});
            skLineSegment(sketch, "E3.2.3.11", {"start": v(21.1, 23) * mm, "end": v(18.6, 27.34) * mm});
            skLineSegment(sketch, "E3.2.3.12", {"start": v(26.1, 23) * mm, "end": v(21.1, 23) * mm});
            skLineSegment(sketch, "E3.2.3.13", {"start": v(18.6, 27.34) * mm, "end": v(21.1, 31.67) * mm});
            skLineSegment(sketch, "E3.2.4.0", {"start": v(11.44, 17.43) * mm, "end": v(8.94, 21.76) * mm});
            skCircle(sketch, "E3.2.4.1", {"center": v(23.6, 16.18) * mm, "radius": 5 * mm, "construction": true});
            skLineSegment(sketch, "E3.2.4.2", {"start": v(21.1, 20.5) * mm, "end": v(26.1, 20.5) * mm});
            skLineSegment(sketch, "E3.2.4.3", {"start": v(28.6, 16.18) * mm, "end": v(26.1, 11.85) * mm});
            skLineSegment(sketch, "E3.2.4.4", {"start": v(18.94, 21.76) * mm, "end": v(16.44, 17.43) * mm});
            skLineSegment(sketch, "E3.2.4.5", {"start": v(16.44, 26.09) * mm, "end": v(18.94, 21.76) * mm});
            skLineSegment(sketch, "E3.2.4.6", {"start": v(11.44, 26.09) * mm, "end": v(16.44, 26.09) * mm});
            skLineSegment(sketch, "E3.2.4.7", {"start": v(16.44, 17.43) * mm, "end": v(11.44, 17.43) * mm});
            skLineSegment(sketch, "E3.2.4.8", {"start": v(26.1, 20.5) * mm, "end": v(28.6, 16.18) * mm});
            skCircle(sketch, "E3.2.4.9", {"center": v(13.94, 21.76) * mm, "radius": 5 * mm, "construction": true});
            skLineSegment(sketch, "E3.2.4.10", {"start": v(8.94, 21.76) * mm, "end": v(11.44, 26.09) * mm});
            skLineSegment(sketch, "E3.2.4.11", {"start": v(21.1, 11.85) * mm, "end": v(18.6, 16.18) * mm});
            skLineSegment(sketch, "E3.2.4.12", {"start": v(26.1, 11.85) * mm, "end": v(21.1, 11.85) * mm});
            skLineSegment(sketch, "E3.2.4.13", {"start": v(18.6, 16.18) * mm, "end": v(21.1, 20.5) * mm});
            skLineSegment(sketch, "E3.2.5.0", {"start": v(11.44, 6.27) * mm, "end": v(8.94, 10.6) * mm});
            skCircle(sketch, "E3.2.5.1", {"center": v(23.6, 5.02) * mm, "radius": 5 * mm, "construction": true});
            skLineSegment(sketch, "E3.2.5.2", {"start": v(21.1, 9.35) * mm, "end": v(26.1, 9.35) * mm});
            skLineSegment(sketch, "E3.2.5.3", {"start": v(28.6, 5.02) * mm, "end": v(26.1, 0.69) * mm});
            skLineSegment(sketch, "E3.2.5.4", {"start": v(18.94, 10.6) * mm, "end": v(16.44, 6.27) * mm});
            skLineSegment(sketch, "E3.2.5.5", {"start": v(16.44, 14.93) * mm, "end": v(18.94, 10.6) * mm});
            skLineSegment(sketch, "E3.2.5.6", {"start": v(11.44, 14.93) * mm, "end": v(16.44, 14.93) * mm});
            skLineSegment(sketch, "E3.2.5.7", {"start": v(16.44, 6.27) * mm, "end": v(11.44, 6.27) * mm});
            skLineSegment(sketch, "E3.2.5.8", {"start": v(26.1, 9.35) * mm, "end": v(28.6, 5.02) * mm});
            skCircle(sketch, "E3.2.5.9", {"center": v(13.94, 10.6) * mm, "radius": 5 * mm, "construction": true});
            skLineSegment(sketch, "E3.2.5.10", {"start": v(8.94, 10.6) * mm, "end": v(11.44, 14.93) * mm});
            skLineSegment(sketch, "E3.2.5.11", {"start": v(21.1, 0.69) * mm, "end": v(18.6, 5.02) * mm});
            skLineSegment(sketch, "E3.2.5.12", {"start": v(26.1, 0.69) * mm, "end": v(21.1, 0.69) * mm});
            skLineSegment(sketch, "E3.2.5.13", {"start": v(18.6, 5.02) * mm, "end": v(21.1, 9.35) * mm});
            skLineSegment(sketch, "E3.2.6.0", {"start": v(11.44, -4.9) * mm, "end": v(8.94, -0.56) * mm});
            skCircle(sketch, "E3.2.6.1", {"center": v(23.6, -6.14) * mm, "radius": 5 * mm, "construction": true});
            skLineSegment(sketch, "E3.2.6.2", {"start": v(21.1, -1.81) * mm, "end": v(26.1, -1.81) * mm});
            skLineSegment(sketch, "E3.2.6.3", {"start": v(28.6, -6.14) * mm, "end": v(26.1, -10.47) * mm});
            skLineSegment(sketch, "E3.2.6.4", {"start": v(18.94, -0.56) * mm, "end": v(16.44, -4.9) * mm});
            skLineSegment(sketch, "E3.2.6.5", {"start": v(16.44, 3.77) * mm, "end": v(18.94, -0.56) * mm});
            skLineSegment(sketch, "E3.2.6.6", {"start": v(11.44, 3.77) * mm, "end": v(16.44, 3.77) * mm});
            skLineSegment(sketch, "E3.2.6.7", {"start": v(16.44, -4.9) * mm, "end": v(11.44, -4.9) * mm});
            skLineSegment(sketch, "E3.2.6.8", {"start": v(26.1, -1.81) * mm, "end": v(28.6, -6.14) * mm});
            skCircle(sketch, "E3.2.6.9", {"center": v(13.94, -0.56) * mm, "radius": 5 * mm, "construction": true});
            skLineSegment(sketch, "E3.2.6.10", {"start": v(8.94, -0.56) * mm, "end": v(11.44, 3.77) * mm});
            skLineSegment(sketch, "E3.2.6.11", {"start": v(21.1, -10.47) * mm, "end": v(18.6, -6.14) * mm});
            skLineSegment(sketch, "E3.2.6.12", {"start": v(26.1, -10.47) * mm, "end": v(21.1, -10.47) * mm});
            skLineSegment(sketch, "E3.2.6.13", {"start": v(18.6, -6.14) * mm, "end": v(21.1, -1.81) * mm});
            skLineSegment(sketch, "E3.2.7.0", {"start": v(11.44, -16.05) * mm, "end": v(8.94, -11.72) * mm});
            skCircle(sketch, "E3.2.7.1", {"center": v(23.6, -17.3) * mm, "radius": 5 * mm, "construction": true});
            skLineSegment(sketch, "E3.2.7.2", {"start": v(21.1, -12.97) * mm, "end": v(26.1, -12.97) * mm});
            skLineSegment(sketch, "E3.2.7.3", {"start": v(28.6, -17.3) * mm, "end": v(26.1, -21.63) * mm});
            skLineSegment(sketch, "E3.2.7.4", {"start": v(18.94, -11.72) * mm, "end": v(16.44, -16.05) * mm});
            skLineSegment(sketch, "E3.2.7.5", {"start": v(16.44, -7.4) * mm, "end": v(18.94, -11.72) * mm});
            skLineSegment(sketch, "E3.2.7.6", {"start": v(11.44, -7.4) * mm, "end": v(16.44, -7.4) * mm});
            skLineSegment(sketch, "E3.2.7.7", {"start": v(16.44, -16.05) * mm, "end": v(11.44, -16.05) * mm});
            skLineSegment(sketch, "E3.2.7.8", {"start": v(26.1, -12.97) * mm, "end": v(28.6, -17.3) * mm});
            skCircle(sketch, "E3.2.7.9", {"center": v(13.94, -11.72) * mm, "radius": 5 * mm, "construction": true});
            skLineSegment(sketch, "E3.2.7.10", {"start": v(8.94, -11.72) * mm, "end": v(11.44, -7.4) * mm});
            skLineSegment(sketch, "E3.2.7.11", {"start": v(21.1, -21.63) * mm, "end": v(18.6, -17.3) * mm});
            skLineSegment(sketch, "E3.2.7.12", {"start": v(26.1, -21.63) * mm, "end": v(21.1, -21.63) * mm});
            skLineSegment(sketch, "E3.2.7.13", {"start": v(18.6, -17.3) * mm, "end": v(21.1, -12.97) * mm});
            skLineSegment(sketch, "E3.2.8.0", {"start": v(11.44, -27.21) * mm, "end": v(8.94, -22.88) * mm});
            skCircle(sketch, "E3.2.8.1", {"center": v(23.6, -28.46) * mm, "radius": 5 * mm, "construction": true});
            skLineSegment(sketch, "E3.2.8.2", {"start": v(21.1, -24.13) * mm, "end": v(26.1, -24.13) * mm});
            skLineSegment(sketch, "E3.2.8.3", {"start": v(28.6, -28.46) * mm, "end": v(26.1, -32.8) * mm});
            skLineSegment(sketch, "E3.2.8.4", {"start": v(18.94, -22.88) * mm, "end": v(16.44, -27.21) * mm});
            skLineSegment(sketch, "E3.2.8.5", {"start": v(16.44, -18.55) * mm, "end": v(18.94, -22.88) * mm});
            skLineSegment(sketch, "E3.2.8.6", {"start": v(11.44, -18.55) * mm, "end": v(16.44, -18.55) * mm});
            skLineSegment(sketch, "E3.2.8.7", {"start": v(16.44, -27.21) * mm, "end": v(11.44, -27.21) * mm});
            skLineSegment(sketch, "E3.2.8.8", {"start": v(26.1, -24.13) * mm, "end": v(28.6, -28.46) * mm});
            skCircle(sketch, "E3.2.8.9", {"center": v(13.94, -22.88) * mm, "radius": 5 * mm, "construction": true});
            skLineSegment(sketch, "E3.2.8.10", {"start": v(8.94, -22.88) * mm, "end": v(11.44, -18.55) * mm});
            skLineSegment(sketch, "E3.2.8.11", {"start": v(21.1, -32.8) * mm, "end": v(18.6, -28.46) * mm});
            skLineSegment(sketch, "E3.2.8.12", {"start": v(26.1, -32.8) * mm, "end": v(21.1, -32.8) * mm});
            skLineSegment(sketch, "E3.2.8.13", {"start": v(18.6, -28.46) * mm, "end": v(21.1, -24.13) * mm});
            skLineSegment(sketch, "E3.2.9.0", {"start": v(11.44, -38.37) * mm, "end": v(8.94, -34.04) * mm});
            skCircle(sketch, "E3.2.9.1", {"center": v(23.6, -39.62) * mm, "radius": 5 * mm, "construction": true});
            skLineSegment(sketch, "E3.2.9.2", {"start": v(21.1, -35.3) * mm, "end": v(26.1, -35.3) * mm});
            skLineSegment(sketch, "E3.2.9.3", {"start": v(28.6, -39.62) * mm, "end": v(26.1, -43.95) * mm});
            skLineSegment(sketch, "E3.2.9.4", {"start": v(18.94, -34.04) * mm, "end": v(16.44, -38.37) * mm});
            skLineSegment(sketch, "E3.2.9.5", {"start": v(16.44, -29.71) * mm, "end": v(18.94, -34.04) * mm});
            skLineSegment(sketch, "E3.2.9.6", {"start": v(11.44, -29.71) * mm, "end": v(16.44, -29.71) * mm});
            skLineSegment(sketch, "E3.2.9.7", {"start": v(16.44, -38.37) * mm, "end": v(11.44, -38.37) * mm});
            skLineSegment(sketch, "E3.2.9.8", {"start": v(26.1, -35.3) * mm, "end": v(28.6, -39.62) * mm});
            skCircle(sketch, "E3.2.9.9", {"center": v(13.94, -34.04) * mm, "radius": 5 * mm, "construction": true});
            skLineSegment(sketch, "E3.2.9.10", {"start": v(8.94, -34.04) * mm, "end": v(11.44, -29.71) * mm});
            skLineSegment(sketch, "E3.2.9.11", {"start": v(21.1, -43.95) * mm, "end": v(18.6, -39.62) * mm});
            skLineSegment(sketch, "E3.2.9.12", {"start": v(26.1, -43.95) * mm, "end": v(21.1, -43.95) * mm});
            skLineSegment(sketch, "E3.2.9.13", {"start": v(18.6, -39.62) * mm, "end": v(21.1, -35.3) * mm});
            skLineSegment(sketch, "E3.2.10.0", {"start": v(11.44, -49.53) * mm, "end": v(8.94, -45.2) * mm});
            skCircle(sketch, "E3.2.10.1", {"center": v(23.6, -50.78) * mm, "radius": 5 * mm, "construction": true});
            skLineSegment(sketch, "E3.2.10.2", {"start": v(21.1, -46.45) * mm, "end": v(26.1, -46.45) * mm});
            skLineSegment(sketch, "E3.2.10.3", {"start": v(28.6, -50.78) * mm, "end": v(26.1, -55.11) * mm});
            skLineSegment(sketch, "E3.2.10.4", {"start": v(18.94, -45.2) * mm, "end": v(16.44, -49.53) * mm});
            skLineSegment(sketch, "E3.2.10.5", {"start": v(16.44, -40.87) * mm, "end": v(18.94, -45.2) * mm});
            skLineSegment(sketch, "E3.2.10.6", {"start": v(11.44, -40.87) * mm, "end": v(16.44, -40.87) * mm});
            skLineSegment(sketch, "E3.2.10.7", {"start": v(16.44, -49.53) * mm, "end": v(11.44, -49.53) * mm});
            skLineSegment(sketch, "E3.2.10.8", {"start": v(26.1, -46.45) * mm, "end": v(28.6, -50.78) * mm});
            skCircle(sketch, "E3.2.10.9", {"center": v(13.94, -45.2) * mm, "radius": 5 * mm, "construction": true});
            skLineSegment(sketch, "E3.2.10.10", {"start": v(8.94, -45.2) * mm, "end": v(11.44, -40.87) * mm});
            skLineSegment(sketch, "E3.2.10.11", {"start": v(21.1, -55.11) * mm, "end": v(18.6, -50.78) * mm});
            skLineSegment(sketch, "E3.2.10.12", {"start": v(26.1, -55.11) * mm, "end": v(21.1, -55.11) * mm});
            skLineSegment(sketch, "E3.2.10.13", {"start": v(18.6, -50.78) * mm, "end": v(21.1, -46.45) * mm});
            skLineSegment(sketch, "E3.3.0.0", {"start": v(-8.56, 62.07) * mm, "end": v(-11.06, 66.4) * mm});
            skCircle(sketch, "E3.3.0.1", {"center": v(3.6, 60.82) * mm, "radius": 5 * mm, "construction": true});
            skLineSegment(sketch, "E3.3.0.2", {"start": v(1.1, 65.15) * mm, "end": v(6.1, 65.15) * mm});
            skLineSegment(sketch, "E3.3.0.3", {"start": v(8.6, 60.82) * mm, "end": v(6.1, 56.49) * mm});
            skLineSegment(sketch, "E3.3.0.4", {"start": v(-1.06, 66.4) * mm, "end": v(-3.56, 62.07) * mm});
            skLineSegment(sketch, "E3.3.0.5", {"start": v(-3.56, 70.73) * mm, "end": v(-1.06, 66.4) * mm});
            skLineSegment(sketch, "E3.3.0.6", {"start": v(-8.56, 70.73) * mm, "end": v(-3.56, 70.73) * mm});
            skLineSegment(sketch, "E3.3.0.7", {"start": v(-3.56, 62.07) * mm, "end": v(-8.56, 62.07) * mm});
            skLineSegment(sketch, "E3.3.0.8", {"start": v(6.1, 65.15) * mm, "end": v(8.6, 60.82) * mm});
            skCircle(sketch, "E3.3.0.9", {"center": v(-6.06, 66.4) * mm, "radius": 5 * mm, "construction": true});
            skLineSegment(sketch, "E3.3.0.10", {"start": v(-11.06, 66.4) * mm, "end": v(-8.56, 70.73) * mm});
            skLineSegment(sketch, "E3.3.0.11", {"start": v(1.1, 56.49) * mm, "end": v(-1.4, 60.82) * mm});
            skLineSegment(sketch, "E3.3.0.12", {"start": v(6.1, 56.49) * mm, "end": v(1.1, 56.49) * mm});
            skLineSegment(sketch, "E3.3.0.13", {"start": v(-1.4, 60.82) * mm, "end": v(1.1, 65.15) * mm});
            skLineSegment(sketch, "E3.3.1.0", {"start": v(-8.56, 50.9) * mm, "end": v(-11.06, 55.24) * mm});
            skCircle(sketch, "E3.3.1.1", {"center": v(3.6, 49.66) * mm, "radius": 5 * mm, "construction": true});
            skLineSegment(sketch, "E3.3.1.2", {"start": v(1.1, 53.99) * mm, "end": v(6.1, 53.99) * mm});
            skLineSegment(sketch, "E3.3.1.3", {"start": v(8.6, 49.66) * mm, "end": v(6.1, 45.33) * mm});
            skLineSegment(sketch, "E3.3.1.4", {"start": v(-1.06, 55.24) * mm, "end": v(-3.56, 50.9) * mm});
            skLineSegment(sketch, "E3.3.1.5", {"start": v(-3.56, 59.57) * mm, "end": v(-1.06, 55.24) * mm});
            skLineSegment(sketch, "E3.3.1.6", {"start": v(-8.56, 59.57) * mm, "end": v(-3.56, 59.57) * mm});
            skLineSegment(sketch, "E3.3.1.7", {"start": v(-3.56, 50.9) * mm, "end": v(-8.56, 50.9) * mm});
            skLineSegment(sketch, "E3.3.1.8", {"start": v(6.1, 53.99) * mm, "end": v(8.6, 49.66) * mm});
            skCircle(sketch, "E3.3.1.9", {"center": v(-6.06, 55.24) * mm, "radius": 5 * mm, "construction": true});
            skLineSegment(sketch, "E3.3.1.10", {"start": v(-11.06, 55.24) * mm, "end": v(-8.56, 59.57) * mm});
            skLineSegment(sketch, "E3.3.1.11", {"start": v(1.1, 45.33) * mm, "end": v(-1.4, 49.66) * mm});
            skLineSegment(sketch, "E3.3.1.12", {"start": v(6.1, 45.33) * mm, "end": v(1.1, 45.33) * mm});
            skLineSegment(sketch, "E3.3.1.13", {"start": v(-1.4, 49.66) * mm, "end": v(1.1, 53.99) * mm});
            skLineSegment(sketch, "E3.3.2.0", {"start": v(-8.56, 39.75) * mm, "end": v(-11.06, 44.08) * mm});
            skCircle(sketch, "E3.3.2.1", {"center": v(3.6, 38.5) * mm, "radius": 5 * mm, "construction": true});
            skLineSegment(sketch, "E3.3.2.2", {"start": v(1.1, 42.83) * mm, "end": v(6.1, 42.83) * mm});
            skLineSegment(sketch, "E3.3.2.3", {"start": v(8.6, 38.5) * mm, "end": v(6.1, 34.17) * mm});
            skLineSegment(sketch, "E3.3.2.4", {"start": v(-1.06, 44.08) * mm, "end": v(-3.56, 39.75) * mm});
            skLineSegment(sketch, "E3.3.2.5", {"start": v(-3.56, 48.4) * mm, "end": v(-1.06, 44.08) * mm});
            skLineSegment(sketch, "E3.3.2.6", {"start": v(-8.56, 48.4) * mm, "end": v(-3.56, 48.4) * mm});
            skLineSegment(sketch, "E3.3.2.7", {"start": v(-3.56, 39.75) * mm, "end": v(-8.56, 39.75) * mm});
            skLineSegment(sketch, "E3.3.2.8", {"start": v(6.1, 42.83) * mm, "end": v(8.6, 38.5) * mm});
            skCircle(sketch, "E3.3.2.9", {"center": v(-6.06, 44.08) * mm, "radius": 5 * mm, "construction": true});
            skLineSegment(sketch, "E3.3.2.10", {"start": v(-11.06, 44.08) * mm, "end": v(-8.56, 48.4) * mm});
            skLineSegment(sketch, "E3.3.2.11", {"start": v(1.1, 34.17) * mm, "end": v(-1.4, 38.5) * mm});
            skLineSegment(sketch, "E3.3.2.12", {"start": v(6.1, 34.17) * mm, "end": v(1.1, 34.17) * mm});
            skLineSegment(sketch, "E3.3.2.13", {"start": v(-1.4, 38.5) * mm, "end": v(1.1, 42.83) * mm});
            skLineSegment(sketch, "E3.3.3.0", {"start": v(-8.56, 28.59) * mm, "end": v(-11.06, 32.92) * mm});
            skCircle(sketch, "E3.3.3.1", {"center": v(3.6, 27.34) * mm, "radius": 5 * mm, "construction": true});
            skLineSegment(sketch, "E3.3.3.2", {"start": v(1.1, 31.67) * mm, "end": v(6.1, 31.67) * mm});
            skLineSegment(sketch, "E3.3.3.3", {"start": v(8.6, 27.34) * mm, "end": v(6.1, 23) * mm});
            skLineSegment(sketch, "E3.3.3.4", {"start": v(-1.06, 32.92) * mm, "end": v(-3.56, 28.59) * mm});
            skLineSegment(sketch, "E3.3.3.5", {"start": v(-3.56, 37.25) * mm, "end": v(-1.06, 32.92) * mm});
            skLineSegment(sketch, "E3.3.3.6", {"start": v(-8.56, 37.25) * mm, "end": v(-3.56, 37.25) * mm});
            skLineSegment(sketch, "E3.3.3.7", {"start": v(-3.56, 28.59) * mm, "end": v(-8.56, 28.59) * mm});
            skLineSegment(sketch, "E3.3.3.8", {"start": v(6.1, 31.67) * mm, "end": v(8.6, 27.34) * mm});
            skCircle(sketch, "E3.3.3.9", {"center": v(-6.06, 32.92) * mm, "radius": 5 * mm, "construction": true});
            skLineSegment(sketch, "E3.3.3.10", {"start": v(-11.06, 32.92) * mm, "end": v(-8.56, 37.25) * mm});
            skLineSegment(sketch, "E3.3.3.11", {"start": v(1.1, 23) * mm, "end": v(-1.4, 27.34) * mm});
            skLineSegment(sketch, "E3.3.3.12", {"start": v(6.1, 23) * mm, "end": v(1.1, 23) * mm});
            skLineSegment(sketch, "E3.3.3.13", {"start": v(-1.4, 27.34) * mm, "end": v(1.1, 31.67) * mm});
            skLineSegment(sketch, "E3.3.4.0", {"start": v(-8.56, 17.43) * mm, "end": v(-11.06, 21.76) * mm});
            skCircle(sketch, "E3.3.4.1", {"center": v(3.6, 16.18) * mm, "radius": 5 * mm, "construction": true});
            skLineSegment(sketch, "E3.3.4.2", {"start": v(1.1, 20.5) * mm, "end": v(6.1, 20.5) * mm});
            skLineSegment(sketch, "E3.3.4.3", {"start": v(8.6, 16.18) * mm, "end": v(6.1, 11.85) * mm});
            skLineSegment(sketch, "E3.3.4.4", {"start": v(-1.06, 21.76) * mm, "end": v(-3.56, 17.43) * mm});
            skLineSegment(sketch, "E3.3.4.5", {"start": v(-3.56, 26.09) * mm, "end": v(-1.06, 21.76) * mm});
            skLineSegment(sketch, "E3.3.4.6", {"start": v(-8.56, 26.09) * mm, "end": v(-3.56, 26.09) * mm});
            skLineSegment(sketch, "E3.3.4.7", {"start": v(-3.56, 17.43) * mm, "end": v(-8.56, 17.43) * mm});
            skLineSegment(sketch, "E3.3.4.8", {"start": v(6.1, 20.5) * mm, "end": v(8.6, 16.18) * mm});
            skCircle(sketch, "E3.3.4.9", {"center": v(-6.06, 21.76) * mm, "radius": 5 * mm, "construction": true});
            skLineSegment(sketch, "E3.3.4.10", {"start": v(-11.06, 21.76) * mm, "end": v(-8.56, 26.09) * mm});
            skLineSegment(sketch, "E3.3.4.11", {"start": v(1.1, 11.85) * mm, "end": v(-1.4, 16.18) * mm});
            skLineSegment(sketch, "E3.3.4.12", {"start": v(6.1, 11.85) * mm, "end": v(1.1, 11.85) * mm});
            skLineSegment(sketch, "E3.3.4.13", {"start": v(-1.4, 16.18) * mm, "end": v(1.1, 20.5) * mm});
            skLineSegment(sketch, "E3.3.5.0", {"start": v(-8.56, 6.27) * mm, "end": v(-11.06, 10.6) * mm});
            skCircle(sketch, "E3.3.5.1", {"center": v(3.6, 5.02) * mm, "radius": 5 * mm, "construction": true});
            skLineSegment(sketch, "E3.3.5.2", {"start": v(1.1, 9.35) * mm, "end": v(6.1, 9.35) * mm});
            skLineSegment(sketch, "E3.3.5.3", {"start": v(8.6, 5.02) * mm, "end": v(6.1, 0.69) * mm});
            skLineSegment(sketch, "E3.3.5.4", {"start": v(-1.06, 10.6) * mm, "end": v(-3.56, 6.27) * mm});
            skLineSegment(sketch, "E3.3.5.5", {"start": v(-3.56, 14.93) * mm, "end": v(-1.06, 10.6) * mm});
            skLineSegment(sketch, "E3.3.5.6", {"start": v(-8.56, 14.93) * mm, "end": v(-3.56, 14.93) * mm});
            skLineSegment(sketch, "E3.3.5.7", {"start": v(-3.56, 6.27) * mm, "end": v(-8.56, 6.27) * mm});
            skLineSegment(sketch, "E3.3.5.8", {"start": v(6.1, 9.35) * mm, "end": v(8.6, 5.02) * mm});
            skCircle(sketch, "E3.3.5.9", {"center": v(-6.06, 10.6) * mm, "radius": 5 * mm, "construction": true});
            skLineSegment(sketch, "E3.3.5.10", {"start": v(-11.06, 10.6) * mm, "end": v(-8.56, 14.93) * mm});
            skLineSegment(sketch, "E3.3.5.11", {"start": v(1.1, 0.69) * mm, "end": v(-1.4, 5.02) * mm});
            skLineSegment(sketch, "E3.3.5.12", {"start": v(6.1, 0.69) * mm, "end": v(1.1, 0.69) * mm});
            skLineSegment(sketch, "E3.3.5.13", {"start": v(-1.4, 5.02) * mm, "end": v(1.1, 9.35) * mm});
            skLineSegment(sketch, "E3.3.6.0", {"start": v(-8.56, -4.9) * mm, "end": v(-11.06, -0.56) * mm});
            skCircle(sketch, "E3.3.6.1", {"center": v(3.6, -6.14) * mm, "radius": 5 * mm, "construction": true});
            skLineSegment(sketch, "E3.3.6.2", {"start": v(1.1, -1.81) * mm, "end": v(6.1, -1.81) * mm});
            skLineSegment(sketch, "E3.3.6.3", {"start": v(8.6, -6.14) * mm, "end": v(6.1, -10.47) * mm});
            skLineSegment(sketch, "E3.3.6.4", {"start": v(-1.06, -0.56) * mm, "end": v(-3.56, -4.9) * mm});
            skLineSegment(sketch, "E3.3.6.5", {"start": v(-3.56, 3.77) * mm, "end": v(-1.06, -0.56) * mm});
            skLineSegment(sketch, "E3.3.6.6", {"start": v(-8.56, 3.77) * mm, "end": v(-3.56, 3.77) * mm});
            skLineSegment(sketch, "E3.3.6.7", {"start": v(-3.56, -4.9) * mm, "end": v(-8.56, -4.9) * mm});
            skLineSegment(sketch, "E3.3.6.8", {"start": v(6.1, -1.81) * mm, "end": v(8.6, -6.14) * mm});
            skCircle(sketch, "E3.3.6.9", {"center": v(-6.06, -0.56) * mm, "radius": 5 * mm, "construction": true});
            skLineSegment(sketch, "E3.3.6.10", {"start": v(-11.06, -0.56) * mm, "end": v(-8.56, 3.77) * mm});
            skLineSegment(sketch, "E3.3.6.11", {"start": v(1.1, -10.47) * mm, "end": v(-1.4, -6.14) * mm});
            skLineSegment(sketch, "E3.3.6.12", {"start": v(6.1, -10.47) * mm, "end": v(1.1, -10.47) * mm});
            skLineSegment(sketch, "E3.3.6.13", {"start": v(-1.4, -6.14) * mm, "end": v(1.1, -1.81) * mm});
            skLineSegment(sketch, "E3.3.7.0", {"start": v(-8.56, -16.05) * mm, "end": v(-11.06, -11.72) * mm});
            skCircle(sketch, "E3.3.7.1", {"center": v(3.6, -17.3) * mm, "radius": 5 * mm, "construction": true});
            skLineSegment(sketch, "E3.3.7.2", {"start": v(1.1, -12.97) * mm, "end": v(6.1, -12.97) * mm});
            skLineSegment(sketch, "E3.3.7.3", {"start": v(8.6, -17.3) * mm, "end": v(6.1, -21.63) * mm});
            skLineSegment(sketch, "E3.3.7.4", {"start": v(-1.06, -11.72) * mm, "end": v(-3.56, -16.05) * mm});
            skLineSegment(sketch, "E3.3.7.5", {"start": v(-3.56, -7.4) * mm, "end": v(-1.06, -11.72) * mm});
            skLineSegment(sketch, "E3.3.7.6", {"start": v(-8.56, -7.4) * mm, "end": v(-3.56, -7.4) * mm});
            skLineSegment(sketch, "E3.3.7.7", {"start": v(-3.56, -16.05) * mm, "end": v(-8.56, -16.05) * mm});
            skLineSegment(sketch, "E3.3.7.8", {"start": v(6.1, -12.97) * mm, "end": v(8.6, -17.3) * mm});
            skCircle(sketch, "E3.3.7.9", {"center": v(-6.06, -11.72) * mm, "radius": 5 * mm, "construction": true});
            skLineSegment(sketch, "E3.3.7.10", {"start": v(-11.06, -11.72) * mm, "end": v(-8.56, -7.4) * mm});
            skLineSegment(sketch, "E3.3.7.11", {"start": v(1.1, -21.63) * mm, "end": v(-1.4, -17.3) * mm});
            skLineSegment(sketch, "E3.3.7.12", {"start": v(6.1, -21.63) * mm, "end": v(1.1, -21.63) * mm});
            skLineSegment(sketch, "E3.3.7.13", {"start": v(-1.4, -17.3) * mm, "end": v(1.1, -12.97) * mm});
            skLineSegment(sketch, "E3.3.8.0", {"start": v(-8.56, -27.21) * mm, "end": v(-11.06, -22.88) * mm});
            skCircle(sketch, "E3.3.8.1", {"center": v(3.6, -28.46) * mm, "radius": 5 * mm, "construction": true});
            skLineSegment(sketch, "E3.3.8.2", {"start": v(1.1, -24.13) * mm, "end": v(6.1, -24.13) * mm});
            skLineSegment(sketch, "E3.3.8.3", {"start": v(8.6, -28.46) * mm, "end": v(6.1, -32.8) * mm});
            skLineSegment(sketch, "E3.3.8.4", {"start": v(-1.06, -22.88) * mm, "end": v(-3.56, -27.21) * mm});
            skLineSegment(sketch, "E3.3.8.5", {"start": v(-3.56, -18.55) * mm, "end": v(-1.06, -22.88) * mm});
            skLineSegment(sketch, "E3.3.8.6", {"start": v(-8.56, -18.55) * mm, "end": v(-3.56, -18.55) * mm});
            skLineSegment(sketch, "E3.3.8.7", {"start": v(-3.56, -27.21) * mm, "end": v(-8.56, -27.21) * mm});
            skLineSegment(sketch, "E3.3.8.8", {"start": v(6.1, -24.13) * mm, "end": v(8.6, -28.46) * mm});
            skCircle(sketch, "E3.3.8.9", {"center": v(-6.06, -22.88) * mm, "radius": 5 * mm, "construction": true});
            skLineSegment(sketch, "E3.3.8.10", {"start": v(-11.06, -22.88) * mm, "end": v(-8.56, -18.55) * mm});
            skLineSegment(sketch, "E3.3.8.11", {"start": v(1.1, -32.8) * mm, "end": v(-1.4, -28.46) * mm});
            skLineSegment(sketch, "E3.3.8.12", {"start": v(6.1, -32.8) * mm, "end": v(1.1, -32.8) * mm});
            skLineSegment(sketch, "E3.3.8.13", {"start": v(-1.4, -28.46) * mm, "end": v(1.1, -24.13) * mm});
            skLineSegment(sketch, "E3.3.9.0", {"start": v(-8.56, -38.37) * mm, "end": v(-11.06, -34.04) * mm});
            skCircle(sketch, "E3.3.9.1", {"center": v(3.6, -39.62) * mm, "radius": 5 * mm, "construction": true});
            skLineSegment(sketch, "E3.3.9.2", {"start": v(1.1, -35.3) * mm, "end": v(6.1, -35.3) * mm});
            skLineSegment(sketch, "E3.3.9.3", {"start": v(8.6, -39.62) * mm, "end": v(6.1, -43.95) * mm});
            skLineSegment(sketch, "E3.3.9.4", {"start": v(-1.06, -34.04) * mm, "end": v(-3.56, -38.37) * mm});
            skLineSegment(sketch, "E3.3.9.5", {"start": v(-3.56, -29.71) * mm, "end": v(-1.06, -34.04) * mm});
            skLineSegment(sketch, "E3.3.9.6", {"start": v(-8.56, -29.71) * mm, "end": v(-3.56, -29.71) * mm});
            skLineSegment(sketch, "E3.3.9.7", {"start": v(-3.56, -38.37) * mm, "end": v(-8.56, -38.37) * mm});
            skLineSegment(sketch, "E3.3.9.8", {"start": v(6.1, -35.3) * mm, "end": v(8.6, -39.62) * mm});
            skCircle(sketch, "E3.3.9.9", {"center": v(-6.06, -34.04) * mm, "radius": 5 * mm, "construction": true});
            skLineSegment(sketch, "E3.3.9.10", {"start": v(-11.06, -34.04) * mm, "end": v(-8.56, -29.71) * mm});
            skLineSegment(sketch, "E3.3.9.11", {"start": v(1.1, -43.95) * mm, "end": v(-1.4, -39.62) * mm});
            skLineSegment(sketch, "E3.3.9.12", {"start": v(6.1, -43.95) * mm, "end": v(1.1, -43.95) * mm});
            skLineSegment(sketch, "E3.3.9.13", {"start": v(-1.4, -39.62) * mm, "end": v(1.1, -35.3) * mm});
            skLineSegment(sketch, "E3.3.10.0", {"start": v(-8.56, -49.53) * mm, "end": v(-11.06, -45.2) * mm});
            skCircle(sketch, "E3.3.10.1", {"center": v(3.6, -50.78) * mm, "radius": 5 * mm, "construction": true});
            skLineSegment(sketch, "E3.3.10.2", {"start": v(1.1, -46.45) * mm, "end": v(6.1, -46.45) * mm});
            skLineSegment(sketch, "E3.3.10.3", {"start": v(8.6, -50.78) * mm, "end": v(6.1, -55.11) * mm});
            skLineSegment(sketch, "E3.3.10.4", {"start": v(-1.06, -45.2) * mm, "end": v(-3.56, -49.53) * mm});
            skLineSegment(sketch, "E3.3.10.5", {"start": v(-3.56, -40.87) * mm, "end": v(-1.06, -45.2) * mm});
            skLineSegment(sketch, "E3.3.10.6", {"start": v(-8.56, -40.87) * mm, "end": v(-3.56, -40.87) * mm});
            skLineSegment(sketch, "E3.3.10.7", {"start": v(-3.56, -49.53) * mm, "end": v(-8.56, -49.53) * mm});
            skLineSegment(sketch, "E3.3.10.8", {"start": v(6.1, -46.45) * mm, "end": v(8.6, -50.78) * mm});
            skCircle(sketch, "E3.3.10.9", {"center": v(-6.06, -45.2) * mm, "radius": 5 * mm, "construction": true});
            skLineSegment(sketch, "E3.3.10.10", {"start": v(-11.06, -45.2) * mm, "end": v(-8.56, -40.87) * mm});
            skLineSegment(sketch, "E3.3.10.11", {"start": v(1.1, -55.11) * mm, "end": v(-1.4, -50.78) * mm});
            skLineSegment(sketch, "E3.3.10.12", {"start": v(6.1, -55.11) * mm, "end": v(1.1, -55.11) * mm});
            skLineSegment(sketch, "E3.3.10.13", {"start": v(-1.4, -50.78) * mm, "end": v(1.1, -46.45) * mm});
            skLineSegment(sketch, "E3.4.0.0", {"start": v(-28.56, 62.07) * mm, "end": v(-31.06, 66.4) * mm});
            skCircle(sketch, "E3.4.0.1", {"center": v(-16.4, 60.82) * mm, "radius": 5 * mm, "construction": true});
            skLineSegment(sketch, "E3.4.0.2", {"start": v(-18.9, 65.15) * mm, "end": v(-13.9, 65.15) * mm});
            skLineSegment(sketch, "E3.4.0.3", {"start": v(-11.4, 60.82) * mm, "end": v(-13.9, 56.49) * mm});
            skLineSegment(sketch, "E3.4.0.4", {"start": v(-21.06, 66.4) * mm, "end": v(-23.56, 62.07) * mm});
            skLineSegment(sketch, "E3.4.0.5", {"start": v(-23.56, 70.73) * mm, "end": v(-21.06, 66.4) * mm});
            skLineSegment(sketch, "E3.4.0.6", {"start": v(-28.56, 70.73) * mm, "end": v(-23.56, 70.73) * mm});
            skLineSegment(sketch, "E3.4.0.7", {"start": v(-23.56, 62.07) * mm, "end": v(-28.56, 62.07) * mm});
            skLineSegment(sketch, "E3.4.0.8", {"start": v(-13.9, 65.15) * mm, "end": v(-11.4, 60.82) * mm});
            skCircle(sketch, "E3.4.0.9", {"center": v(-26.06, 66.4) * mm, "radius": 5 * mm, "construction": true});
            skLineSegment(sketch, "E3.4.0.10", {"start": v(-31.06, 66.4) * mm, "end": v(-28.56, 70.73) * mm});
            skLineSegment(sketch, "E3.4.0.11", {"start": v(-18.9, 56.49) * mm, "end": v(-21.4, 60.82) * mm});
            skLineSegment(sketch, "E3.4.0.12", {"start": v(-13.9, 56.49) * mm, "end": v(-18.9, 56.49) * mm});
            skLineSegment(sketch, "E3.4.0.13", {"start": v(-21.4, 60.82) * mm, "end": v(-18.9, 65.15) * mm});
            skLineSegment(sketch, "E3.4.1.0", {"start": v(-28.56, 50.9) * mm, "end": v(-31.06, 55.24) * mm});
            skCircle(sketch, "E3.4.1.1", {"center": v(-16.4, 49.66) * mm, "radius": 5 * mm, "construction": true});
            skLineSegment(sketch, "E3.4.1.2", {"start": v(-18.9, 53.99) * mm, "end": v(-13.9, 53.99) * mm});
            skLineSegment(sketch, "E3.4.1.3", {"start": v(-11.4, 49.66) * mm, "end": v(-13.9, 45.33) * mm});
            skLineSegment(sketch, "E3.4.1.4", {"start": v(-21.06, 55.24) * mm, "end": v(-23.56, 50.9) * mm});
            skLineSegment(sketch, "E3.4.1.5", {"start": v(-23.56, 59.57) * mm, "end": v(-21.06, 55.24) * mm});
            skLineSegment(sketch, "E3.4.1.6", {"start": v(-28.56, 59.57) * mm, "end": v(-23.56, 59.57) * mm});
            skLineSegment(sketch, "E3.4.1.7", {"start": v(-23.56, 50.9) * mm, "end": v(-28.56, 50.9) * mm});
            skLineSegment(sketch, "E3.4.1.8", {"start": v(-13.9, 53.99) * mm, "end": v(-11.4, 49.66) * mm});
            skCircle(sketch, "E3.4.1.9", {"center": v(-26.06, 55.24) * mm, "radius": 5 * mm, "construction": true});
            skLineSegment(sketch, "E3.4.1.10", {"start": v(-31.06, 55.24) * mm, "end": v(-28.56, 59.57) * mm});
            skLineSegment(sketch, "E3.4.1.11", {"start": v(-18.9, 45.33) * mm, "end": v(-21.4, 49.66) * mm});
            skLineSegment(sketch, "E3.4.1.12", {"start": v(-13.9, 45.33) * mm, "end": v(-18.9, 45.33) * mm});
            skLineSegment(sketch, "E3.4.1.13", {"start": v(-21.4, 49.66) * mm, "end": v(-18.9, 53.99) * mm});
            skLineSegment(sketch, "E3.4.2.0", {"start": v(-28.56, 39.75) * mm, "end": v(-31.06, 44.08) * mm});
            skCircle(sketch, "E3.4.2.1", {"center": v(-16.4, 38.5) * mm, "radius": 5 * mm, "construction": true});
            skLineSegment(sketch, "E3.4.2.2", {"start": v(-18.9, 42.83) * mm, "end": v(-13.9, 42.83) * mm});
            skLineSegment(sketch, "E3.4.2.3", {"start": v(-11.4, 38.5) * mm, "end": v(-13.9, 34.17) * mm});
            skLineSegment(sketch, "E3.4.2.4", {"start": v(-21.06, 44.08) * mm, "end": v(-23.56, 39.75) * mm});
            skLineSegment(sketch, "E3.4.2.5", {"start": v(-23.56, 48.4) * mm, "end": v(-21.06, 44.08) * mm});
            skLineSegment(sketch, "E3.4.2.6", {"start": v(-28.56, 48.4) * mm, "end": v(-23.56, 48.4) * mm});
            skLineSegment(sketch, "E3.4.2.7", {"start": v(-23.56, 39.75) * mm, "end": v(-28.56, 39.75) * mm});
            skLineSegment(sketch, "E3.4.2.8", {"start": v(-13.9, 42.83) * mm, "end": v(-11.4, 38.5) * mm});
            skCircle(sketch, "E3.4.2.9", {"center": v(-26.06, 44.08) * mm, "radius": 5 * mm, "construction": true});
            skLineSegment(sketch, "E3.4.2.10", {"start": v(-31.06, 44.08) * mm, "end": v(-28.56, 48.4) * mm});
            skLineSegment(sketch, "E3.4.2.11", {"start": v(-18.9, 34.17) * mm, "end": v(-21.4, 38.5) * mm});
            skLineSegment(sketch, "E3.4.2.12", {"start": v(-13.9, 34.17) * mm, "end": v(-18.9, 34.17) * mm});
            skLineSegment(sketch, "E3.4.2.13", {"start": v(-21.4, 38.5) * mm, "end": v(-18.9, 42.83) * mm});
            skLineSegment(sketch, "E3.4.3.0", {"start": v(-28.56, 28.59) * mm, "end": v(-31.06, 32.92) * mm});
            skCircle(sketch, "E3.4.3.1", {"center": v(-16.4, 27.34) * mm, "radius": 5 * mm, "construction": true});
            skLineSegment(sketch, "E3.4.3.2", {"start": v(-18.9, 31.67) * mm, "end": v(-13.9, 31.67) * mm});
            skLineSegment(sketch, "E3.4.3.3", {"start": v(-11.4, 27.34) * mm, "end": v(-13.9, 23) * mm});
            skLineSegment(sketch, "E3.4.3.4", {"start": v(-21.06, 32.92) * mm, "end": v(-23.56, 28.59) * mm});
            skLineSegment(sketch, "E3.4.3.5", {"start": v(-23.56, 37.25) * mm, "end": v(-21.06, 32.92) * mm});
            skLineSegment(sketch, "E3.4.3.6", {"start": v(-28.56, 37.25) * mm, "end": v(-23.56, 37.25) * mm});
            skLineSegment(sketch, "E3.4.3.7", {"start": v(-23.56, 28.59) * mm, "end": v(-28.56, 28.59) * mm});
            skLineSegment(sketch, "E3.4.3.8", {"start": v(-13.9, 31.67) * mm, "end": v(-11.4, 27.34) * mm});
            skCircle(sketch, "E3.4.3.9", {"center": v(-26.06, 32.92) * mm, "radius": 5 * mm, "construction": true});
            skLineSegment(sketch, "E3.4.3.10", {"start": v(-31.06, 32.92) * mm, "end": v(-28.56, 37.25) * mm});
            skLineSegment(sketch, "E3.4.3.11", {"start": v(-18.9, 23) * mm, "end": v(-21.4, 27.34) * mm});
            skLineSegment(sketch, "E3.4.3.12", {"start": v(-13.9, 23) * mm, "end": v(-18.9, 23) * mm});
            skLineSegment(sketch, "E3.4.3.13", {"start": v(-21.4, 27.34) * mm, "end": v(-18.9, 31.67) * mm});
            skLineSegment(sketch, "E3.4.4.0", {"start": v(-28.56, 17.43) * mm, "end": v(-31.06, 21.76) * mm});
            skCircle(sketch, "E3.4.4.1", {"center": v(-16.4, 16.18) * mm, "radius": 5 * mm, "construction": true});
            skLineSegment(sketch, "E3.4.4.2", {"start": v(-18.9, 20.5) * mm, "end": v(-13.9, 20.5) * mm});
            skLineSegment(sketch, "E3.4.4.3", {"start": v(-11.4, 16.18) * mm, "end": v(-13.9, 11.85) * mm});
            skLineSegment(sketch, "E3.4.4.4", {"start": v(-21.06, 21.76) * mm, "end": v(-23.56, 17.43) * mm});
            skLineSegment(sketch, "E3.4.4.5", {"start": v(-23.56, 26.09) * mm, "end": v(-21.06, 21.76) * mm});
            skLineSegment(sketch, "E3.4.4.6", {"start": v(-28.56, 26.09) * mm, "end": v(-23.56, 26.09) * mm});
            skLineSegment(sketch, "E3.4.4.7", {"start": v(-23.56, 17.43) * mm, "end": v(-28.56, 17.43) * mm});
            skLineSegment(sketch, "E3.4.4.8", {"start": v(-13.9, 20.5) * mm, "end": v(-11.4, 16.18) * mm});
            skCircle(sketch, "E3.4.4.9", {"center": v(-26.06, 21.76) * mm, "radius": 5 * mm, "construction": true});
            skLineSegment(sketch, "E3.4.4.10", {"start": v(-31.06, 21.76) * mm, "end": v(-28.56, 26.09) * mm});
            skLineSegment(sketch, "E3.4.4.11", {"start": v(-18.9, 11.85) * mm, "end": v(-21.4, 16.18) * mm});
            skLineSegment(sketch, "E3.4.4.12", {"start": v(-13.9, 11.85) * mm, "end": v(-18.9, 11.85) * mm});
            skLineSegment(sketch, "E3.4.4.13", {"start": v(-21.4, 16.18) * mm, "end": v(-18.9, 20.5) * mm});
            skLineSegment(sketch, "E3.4.5.0", {"start": v(-28.56, 6.27) * mm, "end": v(-31.06, 10.6) * mm});
            skCircle(sketch, "E3.4.5.1", {"center": v(-16.4, 5.02) * mm, "radius": 5 * mm, "construction": true});
            skLineSegment(sketch, "E3.4.5.2", {"start": v(-18.9, 9.35) * mm, "end": v(-13.9, 9.35) * mm});
            skLineSegment(sketch, "E3.4.5.3", {"start": v(-11.4, 5.02) * mm, "end": v(-13.9, 0.69) * mm});
            skLineSegment(sketch, "E3.4.5.4", {"start": v(-21.06, 10.6) * mm, "end": v(-23.56, 6.27) * mm});
            skLineSegment(sketch, "E3.4.5.5", {"start": v(-23.56, 14.93) * mm, "end": v(-21.06, 10.6) * mm});
            skLineSegment(sketch, "E3.4.5.6", {"start": v(-28.56, 14.93) * mm, "end": v(-23.56, 14.93) * mm});
            skLineSegment(sketch, "E3.4.5.7", {"start": v(-23.56, 6.27) * mm, "end": v(-28.56, 6.27) * mm});
            skLineSegment(sketch, "E3.4.5.8", {"start": v(-13.9, 9.35) * mm, "end": v(-11.4, 5.02) * mm});
            skCircle(sketch, "E3.4.5.9", {"center": v(-26.06, 10.6) * mm, "radius": 5 * mm, "construction": true});
            skLineSegment(sketch, "E3.4.5.10", {"start": v(-31.06, 10.6) * mm, "end": v(-28.56, 14.93) * mm});
            skLineSegment(sketch, "E3.4.5.11", {"start": v(-18.9, 0.69) * mm, "end": v(-21.4, 5.02) * mm});
            skLineSegment(sketch, "E3.4.5.12", {"start": v(-13.9, 0.69) * mm, "end": v(-18.9, 0.69) * mm});
            skLineSegment(sketch, "E3.4.5.13", {"start": v(-21.4, 5.02) * mm, "end": v(-18.9, 9.35) * mm});
            skLineSegment(sketch, "E3.4.6.0", {"start": v(-28.56, -4.9) * mm, "end": v(-31.06, -0.56) * mm});
            skCircle(sketch, "E3.4.6.1", {"center": v(-16.4, -6.14) * mm, "radius": 5 * mm, "construction": true});
            skLineSegment(sketch, "E3.4.6.2", {"start": v(-18.9, -1.81) * mm, "end": v(-13.9, -1.81) * mm});
            skLineSegment(sketch, "E3.4.6.3", {"start": v(-11.4, -6.14) * mm, "end": v(-13.9, -10.47) * mm});
            skLineSegment(sketch, "E3.4.6.4", {"start": v(-21.06, -0.56) * mm, "end": v(-23.56, -4.9) * mm});
            skLineSegment(sketch, "E3.4.6.5", {"start": v(-23.56, 3.77) * mm, "end": v(-21.06, -0.56) * mm});
            skLineSegment(sketch, "E3.4.6.6", {"start": v(-28.56, 3.77) * mm, "end": v(-23.56, 3.77) * mm});
            skLineSegment(sketch, "E3.4.6.7", {"start": v(-23.56, -4.9) * mm, "end": v(-28.56, -4.9) * mm});
            skLineSegment(sketch, "E3.4.6.8", {"start": v(-13.9, -1.81) * mm, "end": v(-11.4, -6.14) * mm});
            skCircle(sketch, "E3.4.6.9", {"center": v(-26.06, -0.56) * mm, "radius": 5 * mm, "construction": true});
            skLineSegment(sketch, "E3.4.6.10", {"start": v(-31.06, -0.56) * mm, "end": v(-28.56, 3.77) * mm});
            skLineSegment(sketch, "E3.4.6.11", {"start": v(-18.9, -10.47) * mm, "end": v(-21.4, -6.14) * mm});
            skLineSegment(sketch, "E3.4.6.12", {"start": v(-13.9, -10.47) * mm, "end": v(-18.9, -10.47) * mm});
            skLineSegment(sketch, "E3.4.6.13", {"start": v(-21.4, -6.14) * mm, "end": v(-18.9, -1.81) * mm});
            skLineSegment(sketch, "E3.4.7.0", {"start": v(-28.56, -16.05) * mm, "end": v(-31.06, -11.72) * mm});
            skCircle(sketch, "E3.4.7.1", {"center": v(-16.4, -17.3) * mm, "radius": 5 * mm, "construction": true});
            skLineSegment(sketch, "E3.4.7.2", {"start": v(-18.9, -12.97) * mm, "end": v(-13.9, -12.97) * mm});
            skLineSegment(sketch, "E3.4.7.3", {"start": v(-11.4, -17.3) * mm, "end": v(-13.9, -21.63) * mm});
            skLineSegment(sketch, "E3.4.7.4", {"start": v(-21.06, -11.72) * mm, "end": v(-23.56, -16.05) * mm});
            skLineSegment(sketch, "E3.4.7.5", {"start": v(-23.56, -7.4) * mm, "end": v(-21.06, -11.72) * mm});
            skLineSegment(sketch, "E3.4.7.6", {"start": v(-28.56, -7.4) * mm, "end": v(-23.56, -7.4) * mm});
            skLineSegment(sketch, "E3.4.7.7", {"start": v(-23.56, -16.05) * mm, "end": v(-28.56, -16.05) * mm});
            skLineSegment(sketch, "E3.4.7.8", {"start": v(-13.9, -12.97) * mm, "end": v(-11.4, -17.3) * mm});
            skCircle(sketch, "E3.4.7.9", {"center": v(-26.06, -11.72) * mm, "radius": 5 * mm, "construction": true});
            skLineSegment(sketch, "E3.4.7.10", {"start": v(-31.06, -11.72) * mm, "end": v(-28.56, -7.4) * mm});
            skLineSegment(sketch, "E3.4.7.11", {"start": v(-18.9, -21.63) * mm, "end": v(-21.4, -17.3) * mm});
            skLineSegment(sketch, "E3.4.7.12", {"start": v(-13.9, -21.63) * mm, "end": v(-18.9, -21.63) * mm});
            skLineSegment(sketch, "E3.4.7.13", {"start": v(-21.4, -17.3) * mm, "end": v(-18.9, -12.97) * mm});
            skLineSegment(sketch, "E3.4.8.0", {"start": v(-28.56, -27.21) * mm, "end": v(-31.06, -22.88) * mm});
            skCircle(sketch, "E3.4.8.1", {"center": v(-16.4, -28.46) * mm, "radius": 5 * mm, "construction": true});
            skLineSegment(sketch, "E3.4.8.2", {"start": v(-18.9, -24.13) * mm, "end": v(-13.9, -24.13) * mm});
            skLineSegment(sketch, "E3.4.8.3", {"start": v(-11.4, -28.46) * mm, "end": v(-13.9, -32.8) * mm});
            skLineSegment(sketch, "E3.4.8.4", {"start": v(-21.06, -22.88) * mm, "end": v(-23.56, -27.21) * mm});
            skLineSegment(sketch, "E3.4.8.5", {"start": v(-23.56, -18.55) * mm, "end": v(-21.06, -22.88) * mm});
            skLineSegment(sketch, "E3.4.8.6", {"start": v(-28.56, -18.55) * mm, "end": v(-23.56, -18.55) * mm});
            skLineSegment(sketch, "E3.4.8.7", {"start": v(-23.56, -27.21) * mm, "end": v(-28.56, -27.21) * mm});
            skLineSegment(sketch, "E3.4.8.8", {"start": v(-13.9, -24.13) * mm, "end": v(-11.4, -28.46) * mm});
            skCircle(sketch, "E3.4.8.9", {"center": v(-26.06, -22.88) * mm, "radius": 5 * mm, "construction": true});
            skLineSegment(sketch, "E3.4.8.10", {"start": v(-31.06, -22.88) * mm, "end": v(-28.56, -18.55) * mm});
            skLineSegment(sketch, "E3.4.8.11", {"start": v(-18.9, -32.8) * mm, "end": v(-21.4, -28.46) * mm});
            skLineSegment(sketch, "E3.4.8.12", {"start": v(-13.9, -32.8) * mm, "end": v(-18.9, -32.8) * mm});
            skLineSegment(sketch, "E3.4.8.13", {"start": v(-21.4, -28.46) * mm, "end": v(-18.9, -24.13) * mm});
            skLineSegment(sketch, "E3.4.9.0", {"start": v(-28.56, -38.37) * mm, "end": v(-31.06, -34.04) * mm});
            skCircle(sketch, "E3.4.9.1", {"center": v(-16.4, -39.62) * mm, "radius": 5 * mm, "construction": true});
            skLineSegment(sketch, "E3.4.9.2", {"start": v(-18.9, -35.3) * mm, "end": v(-13.9, -35.3) * mm});
            skLineSegment(sketch, "E3.4.9.3", {"start": v(-11.4, -39.62) * mm, "end": v(-13.9, -43.95) * mm});
            skLineSegment(sketch, "E3.4.9.4", {"start": v(-21.06, -34.04) * mm, "end": v(-23.56, -38.37) * mm});
            skLineSegment(sketch, "E3.4.9.5", {"start": v(-23.56, -29.71) * mm, "end": v(-21.06, -34.04) * mm});
            skLineSegment(sketch, "E3.4.9.6", {"start": v(-28.56, -29.71) * mm, "end": v(-23.56, -29.71) * mm});
            skLineSegment(sketch, "E3.4.9.7", {"start": v(-23.56, -38.37) * mm, "end": v(-28.56, -38.37) * mm});
            skLineSegment(sketch, "E3.4.9.8", {"start": v(-13.9, -35.3) * mm, "end": v(-11.4, -39.62) * mm});
            skCircle(sketch, "E3.4.9.9", {"center": v(-26.06, -34.04) * mm, "radius": 5 * mm, "construction": true});
            skLineSegment(sketch, "E3.4.9.10", {"start": v(-31.06, -34.04) * mm, "end": v(-28.56, -29.71) * mm});
            skLineSegment(sketch, "E3.4.9.11", {"start": v(-18.9, -43.95) * mm, "end": v(-21.4, -39.62) * mm});
            skLineSegment(sketch, "E3.4.9.12", {"start": v(-13.9, -43.95) * mm, "end": v(-18.9, -43.95) * mm});
            skLineSegment(sketch, "E3.4.9.13", {"start": v(-21.4, -39.62) * mm, "end": v(-18.9, -35.3) * mm});
            skLineSegment(sketch, "E3.4.10.0", {"start": v(-28.56, -49.53) * mm, "end": v(-31.06, -45.2) * mm});
            skCircle(sketch, "E3.4.10.1", {"center": v(-16.4, -50.78) * mm, "radius": 5 * mm, "construction": true});
            skLineSegment(sketch, "E3.4.10.2", {"start": v(-18.9, -46.45) * mm, "end": v(-13.9, -46.45) * mm});
            skLineSegment(sketch, "E3.4.10.3", {"start": v(-11.4, -50.78) * mm, "end": v(-13.9, -55.11) * mm});
            skLineSegment(sketch, "E3.4.10.4", {"start": v(-21.06, -45.2) * mm, "end": v(-23.56, -49.53) * mm});
            skLineSegment(sketch, "E3.4.10.5", {"start": v(-23.56, -40.87) * mm, "end": v(-21.06, -45.2) * mm});
            skLineSegment(sketch, "E3.4.10.6", {"start": v(-28.56, -40.87) * mm, "end": v(-23.56, -40.87) * mm});
            skLineSegment(sketch, "E3.4.10.7", {"start": v(-23.56, -49.53) * mm, "end": v(-28.56, -49.53) * mm});
            skLineSegment(sketch, "E3.4.10.8", {"start": v(-13.9, -46.45) * mm, "end": v(-11.4, -50.78) * mm});
            skCircle(sketch, "E3.4.10.9", {"center": v(-26.06, -45.2) * mm, "radius": 5 * mm, "construction": true});
            skLineSegment(sketch, "E3.4.10.10", {"start": v(-31.06, -45.2) * mm, "end": v(-28.56, -40.87) * mm});
            skLineSegment(sketch, "E3.4.10.11", {"start": v(-18.9, -55.11) * mm, "end": v(-21.4, -50.78) * mm});
            skLineSegment(sketch, "E3.4.10.12", {"start": v(-13.9, -55.11) * mm, "end": v(-18.9, -55.11) * mm});
            skLineSegment(sketch, "E3.4.10.13", {"start": v(-21.4, -50.78) * mm, "end": v(-18.9, -46.45) * mm});
            skLineSegment(sketch, "E3.5.0.0", {"start": v(-48.56, 62.07) * mm, "end": v(-51.06, 66.4) * mm});
            skCircle(sketch, "E3.5.0.1", {"center": v(-36.4, 60.82) * mm, "radius": 5 * mm, "construction": true});
            skLineSegment(sketch, "E3.5.0.2", {"start": v(-38.9, 65.15) * mm, "end": v(-33.9, 65.15) * mm});
            skLineSegment(sketch, "E3.5.0.3", {"start": v(-31.4, 60.82) * mm, "end": v(-33.9, 56.49) * mm});
            skLineSegment(sketch, "E3.5.0.4", {"start": v(-41.06, 66.4) * mm, "end": v(-43.56, 62.07) * mm});
            skLineSegment(sketch, "E3.5.0.5", {"start": v(-43.56, 70.73) * mm, "end": v(-41.06, 66.4) * mm});
            skLineSegment(sketch, "E3.5.0.6", {"start": v(-48.56, 70.73) * mm, "end": v(-43.56, 70.73) * mm});
            skLineSegment(sketch, "E3.5.0.7", {"start": v(-43.56, 62.07) * mm, "end": v(-48.56, 62.07) * mm});
            skLineSegment(sketch, "E3.5.0.8", {"start": v(-33.9, 65.15) * mm, "end": v(-31.4, 60.82) * mm});
            skCircle(sketch, "E3.5.0.9", {"center": v(-46.06, 66.4) * mm, "radius": 5 * mm, "construction": true});
            skLineSegment(sketch, "E3.5.0.10", {"start": v(-51.06, 66.4) * mm, "end": v(-48.56, 70.73) * mm});
            skLineSegment(sketch, "E3.5.0.11", {"start": v(-38.9, 56.49) * mm, "end": v(-41.4, 60.82) * mm});
            skLineSegment(sketch, "E3.5.0.12", {"start": v(-33.9, 56.49) * mm, "end": v(-38.9, 56.49) * mm});
            skLineSegment(sketch, "E3.5.0.13", {"start": v(-41.4, 60.82) * mm, "end": v(-38.9, 65.15) * mm});
            skLineSegment(sketch, "E3.5.1.0", {"start": v(-48.56, 50.9) * mm, "end": v(-51.06, 55.24) * mm});
            skCircle(sketch, "E3.5.1.1", {"center": v(-36.4, 49.66) * mm, "radius": 5 * mm, "construction": true});
            skLineSegment(sketch, "E3.5.1.2", {"start": v(-38.9, 53.99) * mm, "end": v(-33.9, 53.99) * mm});
            skLineSegment(sketch, "E3.5.1.3", {"start": v(-31.4, 49.66) * mm, "end": v(-33.9, 45.33) * mm});
            skLineSegment(sketch, "E3.5.1.4", {"start": v(-41.06, 55.24) * mm, "end": v(-43.56, 50.9) * mm});
            skLineSegment(sketch, "E3.5.1.5", {"start": v(-43.56, 59.57) * mm, "end": v(-41.06, 55.24) * mm});
            skLineSegment(sketch, "E3.5.1.6", {"start": v(-48.56, 59.57) * mm, "end": v(-43.56, 59.57) * mm});
            skLineSegment(sketch, "E3.5.1.7", {"start": v(-43.56, 50.9) * mm, "end": v(-48.56, 50.9) * mm});
            skLineSegment(sketch, "E3.5.1.8", {"start": v(-33.9, 53.99) * mm, "end": v(-31.4, 49.66) * mm});
            skCircle(sketch, "E3.5.1.9", {"center": v(-46.06, 55.24) * mm, "radius": 5 * mm, "construction": true});
            skLineSegment(sketch, "E3.5.1.10", {"start": v(-51.06, 55.24) * mm, "end": v(-48.56, 59.57) * mm});
            skLineSegment(sketch, "E3.5.1.11", {"start": v(-38.9, 45.33) * mm, "end": v(-41.4, 49.66) * mm});
            skLineSegment(sketch, "E3.5.1.12", {"start": v(-33.9, 45.33) * mm, "end": v(-38.9, 45.33) * mm});
            skLineSegment(sketch, "E3.5.1.13", {"start": v(-41.4, 49.66) * mm, "end": v(-38.9, 53.99) * mm});
            skLineSegment(sketch, "E3.5.2.0", {"start": v(-48.56, 39.75) * mm, "end": v(-51.06, 44.08) * mm});
            skCircle(sketch, "E3.5.2.1", {"center": v(-36.4, 38.5) * mm, "radius": 5 * mm, "construction": true});
            skLineSegment(sketch, "E3.5.2.2", {"start": v(-38.9, 42.83) * mm, "end": v(-33.9, 42.83) * mm});
            skLineSegment(sketch, "E3.5.2.3", {"start": v(-31.4, 38.5) * mm, "end": v(-33.9, 34.17) * mm});
            skLineSegment(sketch, "E3.5.2.4", {"start": v(-41.06, 44.08) * mm, "end": v(-43.56, 39.75) * mm});
            skLineSegment(sketch, "E3.5.2.5", {"start": v(-43.56, 48.4) * mm, "end": v(-41.06, 44.08) * mm});
            skLineSegment(sketch, "E3.5.2.6", {"start": v(-48.56, 48.4) * mm, "end": v(-43.56, 48.4) * mm});
            skLineSegment(sketch, "E3.5.2.7", {"start": v(-43.56, 39.75) * mm, "end": v(-48.56, 39.75) * mm});
            skLineSegment(sketch, "E3.5.2.8", {"start": v(-33.9, 42.83) * mm, "end": v(-31.4, 38.5) * mm});
            skCircle(sketch, "E3.5.2.9", {"center": v(-46.06, 44.08) * mm, "radius": 5 * mm, "construction": true});
            skLineSegment(sketch, "E3.5.2.10", {"start": v(-51.06, 44.08) * mm, "end": v(-48.56, 48.4) * mm});
            skLineSegment(sketch, "E3.5.2.11", {"start": v(-38.9, 34.17) * mm, "end": v(-41.4, 38.5) * mm});
            skLineSegment(sketch, "E3.5.2.12", {"start": v(-33.9, 34.17) * mm, "end": v(-38.9, 34.17) * mm});
            skLineSegment(sketch, "E3.5.2.13", {"start": v(-41.4, 38.5) * mm, "end": v(-38.9, 42.83) * mm});
            skLineSegment(sketch, "E3.5.3.0", {"start": v(-48.56, 28.59) * mm, "end": v(-51.06, 32.92) * mm});
            skCircle(sketch, "E3.5.3.1", {"center": v(-36.4, 27.34) * mm, "radius": 5 * mm, "construction": true});
            skLineSegment(sketch, "E3.5.3.2", {"start": v(-38.9, 31.67) * mm, "end": v(-33.9, 31.67) * mm});
            skLineSegment(sketch, "E3.5.3.3", {"start": v(-31.4, 27.34) * mm, "end": v(-33.9, 23) * mm});
            skLineSegment(sketch, "E3.5.3.4", {"start": v(-41.06, 32.92) * mm, "end": v(-43.56, 28.59) * mm});
            skLineSegment(sketch, "E3.5.3.5", {"start": v(-43.56, 37.25) * mm, "end": v(-41.06, 32.92) * mm});
            skLineSegment(sketch, "E3.5.3.6", {"start": v(-48.56, 37.25) * mm, "end": v(-43.56, 37.25) * mm});
            skLineSegment(sketch, "E3.5.3.7", {"start": v(-43.56, 28.59) * mm, "end": v(-48.56, 28.59) * mm});
            skLineSegment(sketch, "E3.5.3.8", {"start": v(-33.9, 31.67) * mm, "end": v(-31.4, 27.34) * mm});
            skCircle(sketch, "E3.5.3.9", {"center": v(-46.06, 32.92) * mm, "radius": 5 * mm, "construction": true});
            skLineSegment(sketch, "E3.5.3.10", {"start": v(-51.06, 32.92) * mm, "end": v(-48.56, 37.25) * mm});
            skLineSegment(sketch, "E3.5.3.11", {"start": v(-38.9, 23) * mm, "end": v(-41.4, 27.34) * mm});
            skLineSegment(sketch, "E3.5.3.12", {"start": v(-33.9, 23) * mm, "end": v(-38.9, 23) * mm});
            skLineSegment(sketch, "E3.5.3.13", {"start": v(-41.4, 27.34) * mm, "end": v(-38.9, 31.67) * mm});
            skLineSegment(sketch, "E3.5.4.0", {"start": v(-48.56, 17.43) * mm, "end": v(-51.06, 21.76) * mm});
            skCircle(sketch, "E3.5.4.1", {"center": v(-36.4, 16.18) * mm, "radius": 5 * mm, "construction": true});
            skLineSegment(sketch, "E3.5.4.2", {"start": v(-38.9, 20.5) * mm, "end": v(-33.9, 20.5) * mm});
            skLineSegment(sketch, "E3.5.4.3", {"start": v(-31.4, 16.18) * mm, "end": v(-33.9, 11.85) * mm});
            skLineSegment(sketch, "E3.5.4.4", {"start": v(-41.06, 21.76) * mm, "end": v(-43.56, 17.43) * mm});
            skLineSegment(sketch, "E3.5.4.5", {"start": v(-43.56, 26.09) * mm, "end": v(-41.06, 21.76) * mm});
            skLineSegment(sketch, "E3.5.4.6", {"start": v(-48.56, 26.09) * mm, "end": v(-43.56, 26.09) * mm});
            skLineSegment(sketch, "E3.5.4.7", {"start": v(-43.56, 17.43) * mm, "end": v(-48.56, 17.43) * mm});
            skLineSegment(sketch, "E3.5.4.8", {"start": v(-33.9, 20.5) * mm, "end": v(-31.4, 16.18) * mm});
            skCircle(sketch, "E3.5.4.9", {"center": v(-46.06, 21.76) * mm, "radius": 5 * mm, "construction": true});
            skLineSegment(sketch, "E3.5.4.10", {"start": v(-51.06, 21.76) * mm, "end": v(-48.56, 26.09) * mm});
            skLineSegment(sketch, "E3.5.4.11", {"start": v(-38.9, 11.85) * mm, "end": v(-41.4, 16.18) * mm});
            skLineSegment(sketch, "E3.5.4.12", {"start": v(-33.9, 11.85) * mm, "end": v(-38.9, 11.85) * mm});
            skLineSegment(sketch, "E3.5.4.13", {"start": v(-41.4, 16.18) * mm, "end": v(-38.9, 20.5) * mm});
            skLineSegment(sketch, "E3.5.5.0", {"start": v(-48.56, 6.27) * mm, "end": v(-51.06, 10.6) * mm});
            skCircle(sketch, "E3.5.5.1", {"center": v(-36.4, 5.02) * mm, "radius": 5 * mm, "construction": true});
            skLineSegment(sketch, "E3.5.5.2", {"start": v(-38.9, 9.35) * mm, "end": v(-33.9, 9.35) * mm});
            skLineSegment(sketch, "E3.5.5.3", {"start": v(-31.4, 5.02) * mm, "end": v(-33.9, 0.69) * mm});
            skLineSegment(sketch, "E3.5.5.4", {"start": v(-41.06, 10.6) * mm, "end": v(-43.56, 6.27) * mm});
            skLineSegment(sketch, "E3.5.5.5", {"start": v(-43.56, 14.93) * mm, "end": v(-41.06, 10.6) * mm});
            skLineSegment(sketch, "E3.5.5.6", {"start": v(-48.56, 14.93) * mm, "end": v(-43.56, 14.93) * mm});
            skLineSegment(sketch, "E3.5.5.7", {"start": v(-43.56, 6.27) * mm, "end": v(-48.56, 6.27) * mm});
            skLineSegment(sketch, "E3.5.5.8", {"start": v(-33.9, 9.35) * mm, "end": v(-31.4, 5.02) * mm});
            skCircle(sketch, "E3.5.5.9", {"center": v(-46.06, 10.6) * mm, "radius": 5 * mm, "construction": true});
            skLineSegment(sketch, "E3.5.5.10", {"start": v(-51.06, 10.6) * mm, "end": v(-48.56, 14.93) * mm});
            skLineSegment(sketch, "E3.5.5.11", {"start": v(-38.9, 0.69) * mm, "end": v(-41.4, 5.02) * mm});
            skLineSegment(sketch, "E3.5.5.12", {"start": v(-33.9, 0.69) * mm, "end": v(-38.9, 0.69) * mm});
            skLineSegment(sketch, "E3.5.5.13", {"start": v(-41.4, 5.02) * mm, "end": v(-38.9, 9.35) * mm});
            skLineSegment(sketch, "E3.5.6.0", {"start": v(-48.56, -4.9) * mm, "end": v(-51.06, -0.56) * mm});
            skCircle(sketch, "E3.5.6.1", {"center": v(-36.4, -6.14) * mm, "radius": 5 * mm, "construction": true});
            skLineSegment(sketch, "E3.5.6.2", {"start": v(-38.9, -1.81) * mm, "end": v(-33.9, -1.81) * mm});
            skLineSegment(sketch, "E3.5.6.3", {"start": v(-31.4, -6.14) * mm, "end": v(-33.9, -10.47) * mm});
            skLineSegment(sketch, "E3.5.6.4", {"start": v(-41.06, -0.56) * mm, "end": v(-43.56, -4.9) * mm});
            skLineSegment(sketch, "E3.5.6.5", {"start": v(-43.56, 3.77) * mm, "end": v(-41.06, -0.56) * mm});
            skLineSegment(sketch, "E3.5.6.6", {"start": v(-48.56, 3.77) * mm, "end": v(-43.56, 3.77) * mm});
            skLineSegment(sketch, "E3.5.6.7", {"start": v(-43.56, -4.9) * mm, "end": v(-48.56, -4.9) * mm});
            skLineSegment(sketch, "E3.5.6.8", {"start": v(-33.9, -1.81) * mm, "end": v(-31.4, -6.14) * mm});
            skCircle(sketch, "E3.5.6.9", {"center": v(-46.06, -0.56) * mm, "radius": 5 * mm, "construction": true});
            skLineSegment(sketch, "E3.5.6.10", {"start": v(-51.06, -0.56) * mm, "end": v(-48.56, 3.77) * mm});
            skLineSegment(sketch, "E3.5.6.11", {"start": v(-38.9, -10.47) * mm, "end": v(-41.4, -6.14) * mm});
            skLineSegment(sketch, "E3.5.6.12", {"start": v(-33.9, -10.47) * mm, "end": v(-38.9, -10.47) * mm});
            skLineSegment(sketch, "E3.5.6.13", {"start": v(-41.4, -6.14) * mm, "end": v(-38.9, -1.81) * mm});
            skLineSegment(sketch, "E3.5.7.0", {"start": v(-48.56, -16.05) * mm, "end": v(-51.06, -11.72) * mm});
            skCircle(sketch, "E3.5.7.1", {"center": v(-36.4, -17.3) * mm, "radius": 5 * mm, "construction": true});
            skLineSegment(sketch, "E3.5.7.2", {"start": v(-38.9, -12.97) * mm, "end": v(-33.9, -12.97) * mm});
            skLineSegment(sketch, "E3.5.7.3", {"start": v(-31.4, -17.3) * mm, "end": v(-33.9, -21.63) * mm});
            skLineSegment(sketch, "E3.5.7.4", {"start": v(-41.06, -11.72) * mm, "end": v(-43.56, -16.05) * mm});
            skLineSegment(sketch, "E3.5.7.5", {"start": v(-43.56, -7.4) * mm, "end": v(-41.06, -11.72) * mm});
            skLineSegment(sketch, "E3.5.7.6", {"start": v(-48.56, -7.4) * mm, "end": v(-43.56, -7.4) * mm});
            skLineSegment(sketch, "E3.5.7.7", {"start": v(-43.56, -16.05) * mm, "end": v(-48.56, -16.05) * mm});
            skLineSegment(sketch, "E3.5.7.8", {"start": v(-33.9, -12.97) * mm, "end": v(-31.4, -17.3) * mm});
            skCircle(sketch, "E3.5.7.9", {"center": v(-46.06, -11.72) * mm, "radius": 5 * mm, "construction": true});
            skLineSegment(sketch, "E3.5.7.10", {"start": v(-51.06, -11.72) * mm, "end": v(-48.56, -7.4) * mm});
            skLineSegment(sketch, "E3.5.7.11", {"start": v(-38.9, -21.63) * mm, "end": v(-41.4, -17.3) * mm});
            skLineSegment(sketch, "E3.5.7.12", {"start": v(-33.9, -21.63) * mm, "end": v(-38.9, -21.63) * mm});
            skLineSegment(sketch, "E3.5.7.13", {"start": v(-41.4, -17.3) * mm, "end": v(-38.9, -12.97) * mm});
            skLineSegment(sketch, "E3.5.8.0", {"start": v(-48.56, -27.21) * mm, "end": v(-51.06, -22.88) * mm});
            skCircle(sketch, "E3.5.8.1", {"center": v(-36.4, -28.46) * mm, "radius": 5 * mm, "construction": true});
            skLineSegment(sketch, "E3.5.8.2", {"start": v(-38.9, -24.13) * mm, "end": v(-33.9, -24.13) * mm});
            skLineSegment(sketch, "E3.5.8.3", {"start": v(-31.4, -28.46) * mm, "end": v(-33.9, -32.8) * mm});
            skLineSegment(sketch, "E3.5.8.4", {"start": v(-41.06, -22.88) * mm, "end": v(-43.56, -27.21) * mm});
            skLineSegment(sketch, "E3.5.8.5", {"start": v(-43.56, -18.55) * mm, "end": v(-41.06, -22.88) * mm});
            skLineSegment(sketch, "E3.5.8.6", {"start": v(-48.56, -18.55) * mm, "end": v(-43.56, -18.55) * mm});
            skLineSegment(sketch, "E3.5.8.7", {"start": v(-43.56, -27.21) * mm, "end": v(-48.56, -27.21) * mm});
            skLineSegment(sketch, "E3.5.8.8", {"start": v(-33.9, -24.13) * mm, "end": v(-31.4, -28.46) * mm});
            skCircle(sketch, "E3.5.8.9", {"center": v(-46.06, -22.88) * mm, "radius": 5 * mm, "construction": true});
            skLineSegment(sketch, "E3.5.8.10", {"start": v(-51.06, -22.88) * mm, "end": v(-48.56, -18.55) * mm});
            skLineSegment(sketch, "E3.5.8.11", {"start": v(-38.9, -32.8) * mm, "end": v(-41.4, -28.46) * mm});
            skLineSegment(sketch, "E3.5.8.12", {"start": v(-33.9, -32.8) * mm, "end": v(-38.9, -32.8) * mm});
            skLineSegment(sketch, "E3.5.8.13", {"start": v(-41.4, -28.46) * mm, "end": v(-38.9, -24.13) * mm});
            skLineSegment(sketch, "E3.5.9.0", {"start": v(-48.56, -38.37) * mm, "end": v(-51.06, -34.04) * mm});
            skCircle(sketch, "E3.5.9.1", {"center": v(-36.4, -39.62) * mm, "radius": 5 * mm, "construction": true});
            skLineSegment(sketch, "E3.5.9.2", {"start": v(-38.9, -35.3) * mm, "end": v(-33.9, -35.3) * mm});
            skLineSegment(sketch, "E3.5.9.3", {"start": v(-31.4, -39.62) * mm, "end": v(-33.9, -43.95) * mm});
            skLineSegment(sketch, "E3.5.9.4", {"start": v(-41.06, -34.04) * mm, "end": v(-43.56, -38.37) * mm});
            skLineSegment(sketch, "E3.5.9.5", {"start": v(-43.56, -29.71) * mm, "end": v(-41.06, -34.04) * mm});
            skLineSegment(sketch, "E3.5.9.6", {"start": v(-48.56, -29.71) * mm, "end": v(-43.56, -29.71) * mm});
            skLineSegment(sketch, "E3.5.9.7", {"start": v(-43.56, -38.37) * mm, "end": v(-48.56, -38.37) * mm});
            skLineSegment(sketch, "E3.5.9.8", {"start": v(-33.9, -35.3) * mm, "end": v(-31.4, -39.62) * mm});
            skCircle(sketch, "E3.5.9.9", {"center": v(-46.06, -34.04) * mm, "radius": 5 * mm, "construction": true});
            skLineSegment(sketch, "E3.5.9.10", {"start": v(-51.06, -34.04) * mm, "end": v(-48.56, -29.71) * mm});
            skLineSegment(sketch, "E3.5.9.11", {"start": v(-38.9, -43.95) * mm, "end": v(-41.4, -39.62) * mm});
            skLineSegment(sketch, "E3.5.9.12", {"start": v(-33.9, -43.95) * mm, "end": v(-38.9, -43.95) * mm});
            skLineSegment(sketch, "E3.5.9.13", {"start": v(-41.4, -39.62) * mm, "end": v(-38.9, -35.3) * mm});
            skLineSegment(sketch, "E3.5.10.0", {"start": v(-48.56, -49.53) * mm, "end": v(-51.06, -45.2) * mm});
            skCircle(sketch, "E3.5.10.1", {"center": v(-36.4, -50.78) * mm, "radius": 5 * mm, "construction": true});
            skLineSegment(sketch, "E3.5.10.2", {"start": v(-38.9, -46.45) * mm, "end": v(-33.9, -46.45) * mm});
            skLineSegment(sketch, "E3.5.10.3", {"start": v(-31.4, -50.78) * mm, "end": v(-33.9, -55.11) * mm});
            skLineSegment(sketch, "E3.5.10.4", {"start": v(-41.06, -45.2) * mm, "end": v(-43.56, -49.53) * mm});
            skLineSegment(sketch, "E3.5.10.5", {"start": v(-43.56, -40.87) * mm, "end": v(-41.06, -45.2) * mm});
            skLineSegment(sketch, "E3.5.10.6", {"start": v(-48.56, -40.87) * mm, "end": v(-43.56, -40.87) * mm});
            skLineSegment(sketch, "E3.5.10.7", {"start": v(-43.56, -49.53) * mm, "end": v(-48.56, -49.53) * mm});
            skLineSegment(sketch, "E3.5.10.8", {"start": v(-33.9, -46.45) * mm, "end": v(-31.4, -50.78) * mm});
            skCircle(sketch, "E3.5.10.9", {"center": v(-46.06, -45.2) * mm, "radius": 5 * mm, "construction": true});
            skLineSegment(sketch, "E3.5.10.10", {"start": v(-51.06, -45.2) * mm, "end": v(-48.56, -40.87) * mm});
            skLineSegment(sketch, "E3.5.10.11", {"start": v(-38.9, -55.11) * mm, "end": v(-41.4, -50.78) * mm});
            skLineSegment(sketch, "E3.5.10.12", {"start": v(-33.9, -55.11) * mm, "end": v(-38.9, -55.11) * mm});
            skLineSegment(sketch, "E3.5.10.13", {"start": v(-41.4, -50.78) * mm, "end": v(-38.9, -46.45) * mm});
            skLineSegment(sketch, "E3.6.0.0", {"start": v(-68.56, 62.07) * mm, "end": v(-71.06, 66.4) * mm});
            skCircle(sketch, "E3.6.0.1", {"center": v(-56.4, 60.82) * mm, "radius": 5 * mm, "construction": true});
            skLineSegment(sketch, "E3.6.0.2", {"start": v(-58.9, 65.15) * mm, "end": v(-53.9, 65.15) * mm});
            skLineSegment(sketch, "E3.6.0.3", {"start": v(-51.4, 60.82) * mm, "end": v(-53.9, 56.49) * mm});
            skLineSegment(sketch, "E3.6.0.4", {"start": v(-61.06, 66.4) * mm, "end": v(-63.56, 62.07) * mm});
            skLineSegment(sketch, "E3.6.0.5", {"start": v(-63.56, 70.73) * mm, "end": v(-61.06, 66.4) * mm});
            skLineSegment(sketch, "E3.6.0.6", {"start": v(-68.56, 70.73) * mm, "end": v(-63.56, 70.73) * mm});
            skLineSegment(sketch, "E3.6.0.7", {"start": v(-63.56, 62.07) * mm, "end": v(-68.56, 62.07) * mm});
            skLineSegment(sketch, "E3.6.0.8", {"start": v(-53.9, 65.15) * mm, "end": v(-51.4, 60.82) * mm});
            skCircle(sketch, "E3.6.0.9", {"center": v(-66.06, 66.4) * mm, "radius": 5 * mm, "construction": true});
            skLineSegment(sketch, "E3.6.0.10", {"start": v(-71.06, 66.4) * mm, "end": v(-68.56, 70.73) * mm});
            skLineSegment(sketch, "E3.6.0.11", {"start": v(-58.9, 56.49) * mm, "end": v(-61.4, 60.82) * mm});
            skLineSegment(sketch, "E3.6.0.12", {"start": v(-53.9, 56.49) * mm, "end": v(-58.9, 56.49) * mm});
            skLineSegment(sketch, "E3.6.0.13", {"start": v(-61.4, 60.82) * mm, "end": v(-58.9, 65.15) * mm});
            skLineSegment(sketch, "E3.6.1.0", {"start": v(-68.56, 50.9) * mm, "end": v(-71.06, 55.24) * mm});
            skCircle(sketch, "E3.6.1.1", {"center": v(-56.4, 49.66) * mm, "radius": 5 * mm, "construction": true});
            skLineSegment(sketch, "E3.6.1.2", {"start": v(-58.9, 53.99) * mm, "end": v(-53.9, 53.99) * mm});
            skLineSegment(sketch, "E3.6.1.3", {"start": v(-51.4, 49.66) * mm, "end": v(-53.9, 45.33) * mm});
            skLineSegment(sketch, "E3.6.1.4", {"start": v(-61.06, 55.24) * mm, "end": v(-63.56, 50.9) * mm});
            skLineSegment(sketch, "E3.6.1.5", {"start": v(-63.56, 59.57) * mm, "end": v(-61.06, 55.24) * mm});
            skLineSegment(sketch, "E3.6.1.6", {"start": v(-68.56, 59.57) * mm, "end": v(-63.56, 59.57) * mm});
            skLineSegment(sketch, "E3.6.1.7", {"start": v(-63.56, 50.9) * mm, "end": v(-68.56, 50.9) * mm});
            skLineSegment(sketch, "E3.6.1.8", {"start": v(-53.9, 53.99) * mm, "end": v(-51.4, 49.66) * mm});
            skCircle(sketch, "E3.6.1.9", {"center": v(-66.06, 55.24) * mm, "radius": 5 * mm, "construction": true});
            skLineSegment(sketch, "E3.6.1.10", {"start": v(-71.06, 55.24) * mm, "end": v(-68.56, 59.57) * mm});
            skLineSegment(sketch, "E3.6.1.11", {"start": v(-58.9, 45.33) * mm, "end": v(-61.4, 49.66) * mm});
            skLineSegment(sketch, "E3.6.1.12", {"start": v(-53.9, 45.33) * mm, "end": v(-58.9, 45.33) * mm});
            skLineSegment(sketch, "E3.6.1.13", {"start": v(-61.4, 49.66) * mm, "end": v(-58.9, 53.99) * mm});
            skLineSegment(sketch, "E3.6.2.0", {"start": v(-68.56, 39.75) * mm, "end": v(-71.06, 44.08) * mm});
            skCircle(sketch, "E3.6.2.1", {"center": v(-56.4, 38.5) * mm, "radius": 5 * mm, "construction": true});
            skLineSegment(sketch, "E3.6.2.2", {"start": v(-58.9, 42.83) * mm, "end": v(-53.9, 42.83) * mm});
            skLineSegment(sketch, "E3.6.2.3", {"start": v(-51.4, 38.5) * mm, "end": v(-53.9, 34.17) * mm});
            skLineSegment(sketch, "E3.6.2.4", {"start": v(-61.06, 44.08) * mm, "end": v(-63.56, 39.75) * mm});
            skLineSegment(sketch, "E3.6.2.5", {"start": v(-63.56, 48.4) * mm, "end": v(-61.06, 44.08) * mm});
            skLineSegment(sketch, "E3.6.2.6", {"start": v(-68.56, 48.4) * mm, "end": v(-63.56, 48.4) * mm});
            skLineSegment(sketch, "E3.6.2.7", {"start": v(-63.56, 39.75) * mm, "end": v(-68.56, 39.75) * mm});
            skLineSegment(sketch, "E3.6.2.8", {"start": v(-53.9, 42.83) * mm, "end": v(-51.4, 38.5) * mm});
            skCircle(sketch, "E3.6.2.9", {"center": v(-66.06, 44.08) * mm, "radius": 5 * mm, "construction": true});
            skLineSegment(sketch, "E3.6.2.10", {"start": v(-71.06, 44.08) * mm, "end": v(-68.56, 48.4) * mm});
            skLineSegment(sketch, "E3.6.2.11", {"start": v(-58.9, 34.17) * mm, "end": v(-61.4, 38.5) * mm});
            skLineSegment(sketch, "E3.6.2.12", {"start": v(-53.9, 34.17) * mm, "end": v(-58.9, 34.17) * mm});
            skLineSegment(sketch, "E3.6.2.13", {"start": v(-61.4, 38.5) * mm, "end": v(-58.9, 42.83) * mm});
            skLineSegment(sketch, "E3.6.3.0", {"start": v(-68.56, 28.59) * mm, "end": v(-71.06, 32.92) * mm});
            skCircle(sketch, "E3.6.3.1", {"center": v(-56.4, 27.34) * mm, "radius": 5 * mm, "construction": true});
            skLineSegment(sketch, "E3.6.3.2", {"start": v(-58.9, 31.67) * mm, "end": v(-53.9, 31.67) * mm});
            skLineSegment(sketch, "E3.6.3.3", {"start": v(-51.4, 27.34) * mm, "end": v(-53.9, 23) * mm});
            skLineSegment(sketch, "E3.6.3.4", {"start": v(-61.06, 32.92) * mm, "end": v(-63.56, 28.59) * mm});
            skLineSegment(sketch, "E3.6.3.5", {"start": v(-63.56, 37.25) * mm, "end": v(-61.06, 32.92) * mm});
            skLineSegment(sketch, "E3.6.3.6", {"start": v(-68.56, 37.25) * mm, "end": v(-63.56, 37.25) * mm});
            skLineSegment(sketch, "E3.6.3.7", {"start": v(-63.56, 28.59) * mm, "end": v(-68.56, 28.59) * mm});
            skLineSegment(sketch, "E3.6.3.8", {"start": v(-53.9, 31.67) * mm, "end": v(-51.4, 27.34) * mm});
            skCircle(sketch, "E3.6.3.9", {"center": v(-66.06, 32.92) * mm, "radius": 5 * mm, "construction": true});
            skLineSegment(sketch, "E3.6.3.10", {"start": v(-71.06, 32.92) * mm, "end": v(-68.56, 37.25) * mm});
            skLineSegment(sketch, "E3.6.3.11", {"start": v(-58.9, 23) * mm, "end": v(-61.4, 27.34) * mm});
            skLineSegment(sketch, "E3.6.3.12", {"start": v(-53.9, 23) * mm, "end": v(-58.9, 23) * mm});
            skLineSegment(sketch, "E3.6.3.13", {"start": v(-61.4, 27.34) * mm, "end": v(-58.9, 31.67) * mm});
            skLineSegment(sketch, "E3.6.4.0", {"start": v(-68.56, 17.43) * mm, "end": v(-71.06, 21.76) * mm});
            skCircle(sketch, "E3.6.4.1", {"center": v(-56.4, 16.18) * mm, "radius": 5 * mm, "construction": true});
            skLineSegment(sketch, "E3.6.4.2", {"start": v(-58.9, 20.5) * mm, "end": v(-53.9, 20.5) * mm});
            skLineSegment(sketch, "E3.6.4.3", {"start": v(-51.4, 16.18) * mm, "end": v(-53.9, 11.85) * mm});
            skLineSegment(sketch, "E3.6.4.4", {"start": v(-61.06, 21.76) * mm, "end": v(-63.56, 17.43) * mm});
            skLineSegment(sketch, "E3.6.4.5", {"start": v(-63.56, 26.09) * mm, "end": v(-61.06, 21.76) * mm});
            skLineSegment(sketch, "E3.6.4.6", {"start": v(-68.56, 26.09) * mm, "end": v(-63.56, 26.09) * mm});
            skLineSegment(sketch, "E3.6.4.7", {"start": v(-63.56, 17.43) * mm, "end": v(-68.56, 17.43) * mm});
            skLineSegment(sketch, "E3.6.4.8", {"start": v(-53.9, 20.5) * mm, "end": v(-51.4, 16.18) * mm});
            skCircle(sketch, "E3.6.4.9", {"center": v(-66.06, 21.76) * mm, "radius": 5 * mm, "construction": true});
            skLineSegment(sketch, "E3.6.4.10", {"start": v(-71.06, 21.76) * mm, "end": v(-68.56, 26.09) * mm});
            skLineSegment(sketch, "E3.6.4.11", {"start": v(-58.9, 11.85) * mm, "end": v(-61.4, 16.18) * mm});
            skLineSegment(sketch, "E3.6.4.12", {"start": v(-53.9, 11.85) * mm, "end": v(-58.9, 11.85) * mm});
            skLineSegment(sketch, "E3.6.4.13", {"start": v(-61.4, 16.18) * mm, "end": v(-58.9, 20.5) * mm});
            skLineSegment(sketch, "E3.6.5.0", {"start": v(-68.56, 6.27) * mm, "end": v(-71.06, 10.6) * mm});
            skCircle(sketch, "E3.6.5.1", {"center": v(-56.4, 5.02) * mm, "radius": 5 * mm, "construction": true});
            skLineSegment(sketch, "E3.6.5.2", {"start": v(-58.9, 9.35) * mm, "end": v(-53.9, 9.35) * mm});
            skLineSegment(sketch, "E3.6.5.3", {"start": v(-51.4, 5.02) * mm, "end": v(-53.9, 0.69) * mm});
            skLineSegment(sketch, "E3.6.5.4", {"start": v(-61.06, 10.6) * mm, "end": v(-63.56, 6.27) * mm});
            skLineSegment(sketch, "E3.6.5.5", {"start": v(-63.56, 14.93) * mm, "end": v(-61.06, 10.6) * mm});
            skLineSegment(sketch, "E3.6.5.6", {"start": v(-68.56, 14.93) * mm, "end": v(-63.56, 14.93) * mm});
            skLineSegment(sketch, "E3.6.5.7", {"start": v(-63.56, 6.27) * mm, "end": v(-68.56, 6.27) * mm});
            skLineSegment(sketch, "E3.6.5.8", {"start": v(-53.9, 9.35) * mm, "end": v(-51.4, 5.02) * mm});
            skCircle(sketch, "E3.6.5.9", {"center": v(-66.06, 10.6) * mm, "radius": 5 * mm, "construction": true});
            skLineSegment(sketch, "E3.6.5.10", {"start": v(-71.06, 10.6) * mm, "end": v(-68.56, 14.93) * mm});
            skLineSegment(sketch, "E3.6.5.11", {"start": v(-58.9, 0.69) * mm, "end": v(-61.4, 5.02) * mm});
            skLineSegment(sketch, "E3.6.5.12", {"start": v(-53.9, 0.69) * mm, "end": v(-58.9, 0.69) * mm});
            skLineSegment(sketch, "E3.6.5.13", {"start": v(-61.4, 5.02) * mm, "end": v(-58.9, 9.35) * mm});
            skLineSegment(sketch, "E3.6.6.0", {"start": v(-68.56, -4.9) * mm, "end": v(-71.06, -0.56) * mm});
            skCircle(sketch, "E3.6.6.1", {"center": v(-56.4, -6.14) * mm, "radius": 5 * mm, "construction": true});
            skLineSegment(sketch, "E3.6.6.2", {"start": v(-58.9, -1.81) * mm, "end": v(-53.9, -1.81) * mm});
            skLineSegment(sketch, "E3.6.6.3", {"start": v(-51.4, -6.14) * mm, "end": v(-53.9, -10.47) * mm});
            skLineSegment(sketch, "E3.6.6.4", {"start": v(-61.06, -0.56) * mm, "end": v(-63.56, -4.9) * mm});
            skLineSegment(sketch, "E3.6.6.5", {"start": v(-63.56, 3.77) * mm, "end": v(-61.06, -0.56) * mm});
            skLineSegment(sketch, "E3.6.6.6", {"start": v(-68.56, 3.77) * mm, "end": v(-63.56, 3.77) * mm});
            skLineSegment(sketch, "E3.6.6.7", {"start": v(-63.56, -4.9) * mm, "end": v(-68.56, -4.9) * mm});
            skLineSegment(sketch, "E3.6.6.8", {"start": v(-53.9, -1.81) * mm, "end": v(-51.4, -6.14) * mm});
            skCircle(sketch, "E3.6.6.9", {"center": v(-66.06, -0.56) * mm, "radius": 5 * mm, "construction": true});
            skLineSegment(sketch, "E3.6.6.10", {"start": v(-71.06, -0.56) * mm, "end": v(-68.56, 3.77) * mm});
            skLineSegment(sketch, "E3.6.6.11", {"start": v(-58.9, -10.47) * mm, "end": v(-61.4, -6.14) * mm});
            skLineSegment(sketch, "E3.6.6.12", {"start": v(-53.9, -10.47) * mm, "end": v(-58.9, -10.47) * mm});
            skLineSegment(sketch, "E3.6.6.13", {"start": v(-61.4, -6.14) * mm, "end": v(-58.9, -1.81) * mm});
            skLineSegment(sketch, "E3.6.7.0", {"start": v(-68.56, -16.05) * mm, "end": v(-71.06, -11.72) * mm});
            skCircle(sketch, "E3.6.7.1", {"center": v(-56.4, -17.3) * mm, "radius": 5 * mm, "construction": true});
            skLineSegment(sketch, "E3.6.7.2", {"start": v(-58.9, -12.97) * mm, "end": v(-53.9, -12.97) * mm});
            skLineSegment(sketch, "E3.6.7.3", {"start": v(-51.4, -17.3) * mm, "end": v(-53.9, -21.63) * mm});
            skLineSegment(sketch, "E3.6.7.4", {"start": v(-61.06, -11.72) * mm, "end": v(-63.56, -16.05) * mm});
            skLineSegment(sketch, "E3.6.7.5", {"start": v(-63.56, -7.4) * mm, "end": v(-61.06, -11.72) * mm});
            skLineSegment(sketch, "E3.6.7.6", {"start": v(-68.56, -7.4) * mm, "end": v(-63.56, -7.4) * mm});
            skLineSegment(sketch, "E3.6.7.7", {"start": v(-63.56, -16.05) * mm, "end": v(-68.56, -16.05) * mm});
            skLineSegment(sketch, "E3.6.7.8", {"start": v(-53.9, -12.97) * mm, "end": v(-51.4, -17.3) * mm});
            skCircle(sketch, "E3.6.7.9", {"center": v(-66.06, -11.72) * mm, "radius": 5 * mm, "construction": true});
            skLineSegment(sketch, "E3.6.7.10", {"start": v(-71.06, -11.72) * mm, "end": v(-68.56, -7.4) * mm});
            skLineSegment(sketch, "E3.6.7.11", {"start": v(-58.9, -21.63) * mm, "end": v(-61.4, -17.3) * mm});
            skLineSegment(sketch, "E3.6.7.12", {"start": v(-53.9, -21.63) * mm, "end": v(-58.9, -21.63) * mm});
            skLineSegment(sketch, "E3.6.7.13", {"start": v(-61.4, -17.3) * mm, "end": v(-58.9, -12.97) * mm});
            skLineSegment(sketch, "E3.6.8.0", {"start": v(-68.56, -27.21) * mm, "end": v(-71.06, -22.88) * mm});
            skCircle(sketch, "E3.6.8.1", {"center": v(-56.4, -28.46) * mm, "radius": 5 * mm, "construction": true});
            skLineSegment(sketch, "E3.6.8.2", {"start": v(-58.9, -24.13) * mm, "end": v(-53.9, -24.13) * mm});
            skLineSegment(sketch, "E3.6.8.3", {"start": v(-51.4, -28.46) * mm, "end": v(-53.9, -32.8) * mm});
            skLineSegment(sketch, "E3.6.8.4", {"start": v(-61.06, -22.88) * mm, "end": v(-63.56, -27.21) * mm});
            skLineSegment(sketch, "E3.6.8.5", {"start": v(-63.56, -18.55) * mm, "end": v(-61.06, -22.88) * mm});
            skLineSegment(sketch, "E3.6.8.6", {"start": v(-68.56, -18.55) * mm, "end": v(-63.56, -18.55) * mm});
            skLineSegment(sketch, "E3.6.8.7", {"start": v(-63.56, -27.21) * mm, "end": v(-68.56, -27.21) * mm});
            skLineSegment(sketch, "E3.6.8.8", {"start": v(-53.9, -24.13) * mm, "end": v(-51.4, -28.46) * mm});
            skCircle(sketch, "E3.6.8.9", {"center": v(-66.06, -22.88) * mm, "radius": 5 * mm, "construction": true});
            skLineSegment(sketch, "E3.6.8.10", {"start": v(-71.06, -22.88) * mm, "end": v(-68.56, -18.55) * mm});
            skLineSegment(sketch, "E3.6.8.11", {"start": v(-58.9, -32.8) * mm, "end": v(-61.4, -28.46) * mm});
            skLineSegment(sketch, "E3.6.8.12", {"start": v(-53.9, -32.8) * mm, "end": v(-58.9, -32.8) * mm});
            skLineSegment(sketch, "E3.6.8.13", {"start": v(-61.4, -28.46) * mm, "end": v(-58.9, -24.13) * mm});
            skLineSegment(sketch, "E3.6.9.0", {"start": v(-68.56, -38.37) * mm, "end": v(-71.06, -34.04) * mm});
            skCircle(sketch, "E3.6.9.1", {"center": v(-56.4, -39.62) * mm, "radius": 5 * mm, "construction": true});
            skLineSegment(sketch, "E3.6.9.2", {"start": v(-58.9, -35.3) * mm, "end": v(-53.9, -35.3) * mm});
            skLineSegment(sketch, "E3.6.9.3", {"start": v(-51.4, -39.62) * mm, "end": v(-53.9, -43.95) * mm});
            skLineSegment(sketch, "E3.6.9.4", {"start": v(-61.06, -34.04) * mm, "end": v(-63.56, -38.37) * mm});
            skLineSegment(sketch, "E3.6.9.5", {"start": v(-63.56, -29.71) * mm, "end": v(-61.06, -34.04) * mm});
            skLineSegment(sketch, "E3.6.9.6", {"start": v(-68.56, -29.71) * mm, "end": v(-63.56, -29.71) * mm});
            skLineSegment(sketch, "E3.6.9.7", {"start": v(-63.56, -38.37) * mm, "end": v(-68.56, -38.37) * mm});
            skLineSegment(sketch, "E3.6.9.8", {"start": v(-53.9, -35.3) * mm, "end": v(-51.4, -39.62) * mm});
            skCircle(sketch, "E3.6.9.9", {"center": v(-66.06, -34.04) * mm, "radius": 5 * mm, "construction": true});
            skLineSegment(sketch, "E3.6.9.10", {"start": v(-71.06, -34.04) * mm, "end": v(-68.56, -29.71) * mm});
            skLineSegment(sketch, "E3.6.9.11", {"start": v(-58.9, -43.95) * mm, "end": v(-61.4, -39.62) * mm});
            skLineSegment(sketch, "E3.6.9.12", {"start": v(-53.9, -43.95) * mm, "end": v(-58.9, -43.95) * mm});
            skLineSegment(sketch, "E3.6.9.13", {"start": v(-61.4, -39.62) * mm, "end": v(-58.9, -35.3) * mm});
            skLineSegment(sketch, "E3.6.10.0", {"start": v(-68.56, -49.53) * mm, "end": v(-71.06, -45.2) * mm});
            skCircle(sketch, "E3.6.10.1", {"center": v(-56.4, -50.78) * mm, "radius": 5 * mm, "construction": true});
            skLineSegment(sketch, "E3.6.10.2", {"start": v(-58.9, -46.45) * mm, "end": v(-53.9, -46.45) * mm});
            skLineSegment(sketch, "E3.6.10.3", {"start": v(-51.4, -50.78) * mm, "end": v(-53.9, -55.11) * mm});
            skLineSegment(sketch, "E3.6.10.4", {"start": v(-61.06, -45.2) * mm, "end": v(-63.56, -49.53) * mm});
            skLineSegment(sketch, "E3.6.10.5", {"start": v(-63.56, -40.87) * mm, "end": v(-61.06, -45.2) * mm});
            skLineSegment(sketch, "E3.6.10.6", {"start": v(-68.56, -40.87) * mm, "end": v(-63.56, -40.87) * mm});
            skLineSegment(sketch, "E3.6.10.7", {"start": v(-63.56, -49.53) * mm, "end": v(-68.56, -49.53) * mm});
            skLineSegment(sketch, "E3.6.10.8", {"start": v(-53.9, -46.45) * mm, "end": v(-51.4, -50.78) * mm});
            skCircle(sketch, "E3.6.10.9", {"center": v(-66.06, -45.2) * mm, "radius": 5 * mm, "construction": true});
            skLineSegment(sketch, "E3.6.10.10", {"start": v(-71.06, -45.2) * mm, "end": v(-68.56, -40.87) * mm});
            skLineSegment(sketch, "E3.6.10.11", {"start": v(-58.9, -55.11) * mm, "end": v(-61.4, -50.78) * mm});
            skLineSegment(sketch, "E3.6.10.12", {"start": v(-53.9, -55.11) * mm, "end": v(-58.9, -55.11) * mm});
            skLineSegment(sketch, "E3.6.10.13", {"start": v(-61.4, -50.78) * mm, "end": v(-58.9, -46.45) * mm});
            skLineSegment(sketch, "E3.direction1", {"start": v(51.44, 62.07) * mm, "end": v(31.44, 62.07) * mm, "construction": true});
            skLineSegment(sketch, "E3.direction2", {"start": v(51.44, 62.07) * mm, "end": v(51.44, 50.9) * mm, "construction": true});
            skSolve(sketch);
        }
        {
            var Q0;
            Q0 = qSketchRegion(id + "F2", true);
            extrude(context, id + "F3", {"entities" : qUnion([Q0]), "operationType" : NewBodyOperationType.REMOVE, "oppositeDirection" : true, "depth" : 3 * mm, "offsetDistance" : 25 * mm, "hasDraft" : true, "draftAngle" : 30 * degree, "draftPullDirection" : true});
        }
        {
            var Q0;
            Q0=makeQuery(id+"F1.opExtrude","CAP_FACE",FACE,{"disambiguationData":[OSD([sQuery(id+"F0.wireOp",EDGE,"E0.0"),sQuery(id+"F0.wireOp",EDGE,"E0.1"),sQuery(id+"F0.wireOp",EDGE,"E0.2"),sQuery(id+"F0.wireOp",EDGE,"E0.3"),sQuery(id+"F0.wireOp",EDGE,"E0.4"),sQuery(id+"F0.wireOp",EDGE,"E0.5")])],"isStart":false});
            var sketch = newSketch(context, id + "F4", { "sketchPlane" : qUnion([Q0])});
            skPoint(sketch, "E4", {"position": v(0, 0) * mm});
            skCircle(sketch, "E5.cCircle", {"center": v(0, 0) * mm, "radius": 65.83 * mm, "construction": true});
            skLineSegment(sketch, "E5.0", {"start": v(65.83, 0) * mm, "end": v(32.92, -57.01) * mm});
            skLineSegment(sketch, "E5.1", {"start": v(32.92, -57.01) * mm, "end": v(-32.92, -57.01) * mm});
            skLineSegment(sketch, "E5.2", {"start": v(-32.92, -57.01) * mm, "end": v(-65.83, 0) * mm});
            skLineSegment(sketch, "E5.3", {"start": v(-65.83, 0) * mm, "end": v(-32.92, 57.01) * mm});
            skLineSegment(sketch, "E5.4", {"start": v(-32.92, 57.01) * mm, "end": v(32.92, 57.01) * mm});
            skLineSegment(sketch, "E5.5", {"start": v(32.92, 57.01) * mm, "end": v(65.83, 0) * mm});
            skCircle(sketch, "E6", {"center": v(0, 0) * mm, "radius": 47.5 * mm});
            skSolve(sketch);
        }
        {
            var Q0;
            Q0 = qSketchRegion(id + "F4", true);
            extrude(context, id + "F5", {"entities" : qUnion([Q0]), "operationType" : NewBodyOperationType.ADD, "oppositeDirection" : true, "depth" : 7 * mm, "offsetDistance" : 25 * mm, "hasDraft" : true, "draftAngle" : 22.5 * degree, "draftPullDirection" : true});
        }
        {
            var Q0;
            Q0=makeQuery(id+"F5.opExtrude","SWEPT_EDGE",EDGE,{"disambiguationData":[OSD([sQuery(id+"F4.wireOp",EDGE,"E5.0"),sQuery(id+"F4.wireOp",EDGE,"E5.1")])]});
            var Q1;
            Q1=makeQuery(id+"F5.opExtrude","SWEPT_EDGE",EDGE,{"disambiguationData":[OSD([sQuery(id+"F4.wireOp",EDGE,"E5.1"),sQuery(id+"F4.wireOp",EDGE,"E5.2")])]});
            var Q2;
            Q2=makeQuery(id+"F5.opExtrude","SWEPT_EDGE",EDGE,{"disambiguationData":[OSD([sQuery(id+"F4.wireOp",EDGE,"E5.2"),sQuery(id+"F4.wireOp",EDGE,"E5.3")])]});
            var Q3;
            Q3=makeQuery(id+"F5.opExtrude","SWEPT_EDGE",EDGE,{"disambiguationData":[OSD([sQuery(id+"F4.wireOp",EDGE,"E5.0"),sQuery(id+"F4.wireOp",EDGE,"E5.5")])]});
            var Q4;
            Q4=makeQuery(id+"F5.opExtrude","SWEPT_EDGE",EDGE,{"disambiguationData":[OSD([sQuery(id+"F4.wireOp",EDGE,"E5.3"),sQuery(id+"F4.wireOp",EDGE,"E5.4")])]});
            var Q5;
            Q5=makeQuery(id+"F5.opExtrude","SWEPT_EDGE",EDGE,{"disambiguationData":[OSD([sQuery(id+"F4.wireOp",EDGE,"E5.4"),sQuery(id+"F4.wireOp",EDGE,"E5.5")])]});
            fillet(context, id + "F6", {"entities" : qUnion([Q0, Q1, Q2, Q3, Q4, Q5]), "radius" : 10 * mm, "tangentPropagation" : true, "allowEdgeOverflow" : false});
        }
    });
